FCSTD DOCUMENT  (FreeCAD 0.19R24276 (Git))
Label: Assembly
License: All rights reserved
LicenseURL: http://en.wikipedia.org/wiki/All_rights_reserved
objects: App::Link×6, App::DocumentObjectGroup×2, PartDesign::CoordinateSystem×1, App::FeaturePython×1, App::Part×1
note: 1 computed .brp shape members not serialized (recipe doc carries the construction recipe); baked Part::Feature solids carry a one-line shape summary decoded from their .brp
EXTERNAL_REF file=AssemblyBase.FCStd obj=LCS_Origin
EXTERNAL_REF file=AssemblyBase.FCStd obj=Model
EXTERNAL_REF file=AssemblyArt1.FCStd obj=LCS_Origin
EXTERNAL_REF file=AssemblyBase.FCStd obj=LCS_Art1003
EXTERNAL_REF file=AssemblyArt1.FCStd obj=Model
EXTERNAL_REF file=AssemblyArt1.FCStd obj=LCS_Art2002
EXTERNAL_REF file=AssemblyArt2.FCStd obj=LCS_Art1
EXTERNAL_REF file=AssemblyArt2.FCStd obj=Model
EXTERNAL_REF file=AssemblyArt2.FCStd obj=LCS_Model_1
EXTERNAL_REF file=AssemblyArt3.FCStd obj=LCS_Art2Fix
EXTERNAL_REF file=AssemblyArt3.FCStd obj=Model
EXTERNAL_REF file=AssemblyArt3.FCStd obj=LCS_Art4Fix
EXTERNAL_REF file=AssemblyArt4.FCStd obj=LCS_Art3Fix
EXTERNAL_REF file=AssemblyArt4.FCStd obj=Model
EXTERNAL_REF file=AssemblyArt4.FCStd obj=LCS_Art56Fix
EXTERNAL_REF file=AssemblyArt56.FCStd obj=LCS_Art4Fix
EXTERNAL_REF file=AssemblyArt56.FCStd obj=Model

FEATURE [App::DocumentObjectGroup] Parts
FEATURE [PartDesign::CoordinateSystem] LCS_Origin
  AttacherType = Attacher::AttachEngine3D
  MapMode = 2
  Support = -> [X_Axis]
FEATURE [App::DocumentObjectGroup] Constraints
FEATURE [App::FeaturePython] Variables  # WARN: FeaturePython — macro-defined, semantics opaque (R4)
FEATURE [App::Link] AssemblyBase
  AssemblyType = Asm4EE
  AttachedBy = #LCS_Origin
  AttachedTo = Parent Assembly#LCS_Origin
  LinkedObject = -> <external AssemblyBase.FCStd>#Model
  expr: Placement = LCS_Origin.Placement * AttachmentOffset * AssemblyBase#LCS_Origin.Placement ^ -1
FEATURE [App::Link] AssemblyArt1
  AssemblyType = Asm4EE
  AttachedBy = #LCS_Origin
  AttachedTo = AssemblyBase#LCS_Art1003
  AttachmentOffset = pos=(0,0,0) rot=(0,0,1;4.71239rad)
  LinkPlacement = pos=(0,0,79) rot=(0,0,1;0rad)
  LinkedObject = -> <external AssemblyArt1.FCStd>#Model
  Placement = pos=(0,0,79) rot=(0,0,1;0rad)
  expr: Placement = AssemblyBase.Placement * AssemblyBase#LCS_Art1003.Placement * AttachmentOffset * AssemblyArt1#LCS_Origin.Placement ^ -1
FEATURE [App::Link] AssemblyArt2
  AssemblyType = Asm4EE
  AttachedBy = #LCS_Art1
  AttachedTo = AssemblyArt1#LCS_Art2002
  AttachmentOffset = pos=(0,0,0) rot=(0,0.707107,0.707107;3.14159rad)
  LinkPlacement = pos=(-5.9e-15,-68,202) rot=(0,0.707107,0.707107;3.14159rad)
  LinkedObject = -> <external AssemblyArt2.FCStd>#Model
  Placement = pos=(-5.9e-15,-68,202) rot=(0,0.707107,0.707107;3.14159rad)
  expr: Placement = AssemblyArt1.Placement * AssemblyArt1#LCS_Art2002.Placement * AttachmentOffset * AssemblyArt2#LCS_Art1.Placement ^ -1
FEATURE [App::Link] AssemblyArt3
  AssemblyType = Asm4EE
  AttachedBy = #LCS_Art2Fix
  AttachedTo = AssemblyArt2#LCS_Model_1
  AttachmentOffset = pos=(0,0,0) rot=(1,0,0;1.5708rad)
  LinkPlacement = pos=(-2.09e-14,0,443.5) rot=(0,1,0;3.14159rad)
  LinkedObject = -> <external AssemblyArt3.FCStd>#Model
  Placement = pos=(-2.09e-14,0,443.5) rot=(0,1,0;3.14159rad)
  expr: Placement = AssemblyArt2.Placement * AssemblyArt2#LCS_Model_1.Placement * AttachmentOffset * AssemblyArt3#LCS_Art2Fix.Placement ^ -1
FEATURE [App::Link] AssemblyArt4
  AssemblyType = Asm4EE
  AttachedBy = #LCS_Art3Fix
  AttachedTo = AssemblyArt3#LCS_Art4Fix
  AttachmentOffset = pos=(0,0,0) rot=(0,-1,0;3.14159rad)
  LinkPlacement = pos=(-2.1e-14,0,444.5) rot=(0,0,1;0rad)
  LinkedObject = -> <external AssemblyArt4.FCStd>#Model
  Placement = pos=(-2.1e-14,0,444.5) rot=(0,0,1;0rad)
  expr: Placement = AssemblyArt3.Placement * AssemblyArt3#LCS_Art4Fix.Placement * AttachmentOffset * AssemblyArt4#LCS_Art3Fix.Placement ^ -1
FEATURE [App::Link] AssemblyArt56
  AssemblyType = Asm4EE
  AttachedBy = #LCS_Art4Fix
  AttachedTo = AssemblyArt4#LCS_Art56Fix
  AttachmentOffset = pos=(0,0,0) rot=(0,0,1;1.5708rad)
  LinkPlacement = pos=(-3.07e-14,-1.37e-14,556) rot=(0,0,1;1.5708rad)
  LinkedObject = -> <external AssemblyArt56.FCStd>#Model
  Placement = pos=(-3.07e-14,-1.37e-14,556) rot=(0,0,1;1.5708rad)
  expr: Placement = AssemblyArt4.Placement * AssemblyArt4#LCS_Art56Fix.Placement * AttachmentOffset * AssemblyArt56#LCS_Art4Fix.Placement ^ -1
FEATURE [App::Part] Model
  Configuration = 0
  Group = -> [LCS_Origin,Constraints,Variables,AssemblyBase,AssemblyArt1,AssemblyArt2,AssemblyArt3,AssemblyArt4,AssemblyArt56]
  Origin = -> Origin
  Type = Assembly4 Model

RESOLVED EXTERNAL PARTS (link-assembly join: the EXTERNAL_REF files above that resolve inside this repo's crawl, each included once):
---- part AssemblyArt1.FCStd = doc fcstd_79f823e0a2d4 (58987 chars; too large to inline — full recipe in that document) ----
---- part AssemblyArt2.FCStd = doc fcstd_96a41e5eaa72 (60164 chars; too large to inline — full recipe in that document) ----
---- part AssemblyArt3.FCStd = doc fcstd_8b5b8ba6da66 ----
FCSTD DOCUMENT  (FreeCAD 0.19R24276 (Git))
Label: AssemblyArt3
License: All rights reserved
LicenseURL: http://en.wikipedia.org/wiki/All_rights_reserved
objects: Part::FeaturePython×49, App::Link×14, PartDesign::CoordinateSystem×13, App::Part×7, App::DocumentObjectGroup×6, Part::Feature×5, PartDesign::Line×5, App::FeaturePython×1, Part::Sphere×1
note: 72 computed .brp shape members not serialized (recipe doc carries the construction recipe); baked Part::Feature solids carry a one-line shape summary decoded from their .brp
EXTERNAL_REF file=Art3Body.FCStd obj=LCS_Bottom
EXTERNAL_REF file=Art3Body.FCStd obj=Body002
EXTERNAL_REF file=Art23Optodisk.FCStd obj=LCS_Art23Optodisk
EXTERNAL_REF file=Art3Body.FCStd obj=LCS_OptoDisk
EXTERNAL_REF file=Art23Optodisk.FCStd obj=Body
EXTERNAL_REF file=Art3Body.FCStd obj=LCS_Pulley
EXTERNAL_REF file=Art3Pulley.FCStd obj=LCS_Art3Pulley
EXTERNAL_REF file=Art3Pulley.FCStd obj=Body
EXTERNAL_REF file=Art3Body.FCStd obj=LCS_Art4MotorHolder
EXTERNAL_REF file=Art4MotorFix.FCStd obj=LCS_Art4MotorFix
EXTERNAL_REF file=Art4MotorFix.FCStd obj=Body
EXTERNAL_REF file=Art4MotorFix.FCStd obj=LCS_Art4Motor
EXTERNAL_REF file=Art4MotorGear.FCStd obj=LCS_Art4MotorGear
EXTERNAL_REF file=Art4MotorGear.FCStd obj=Body
EXTERNAL_REF file=Art3Body.FCStd obj=LCS_Fan
EXTERNAL_REF file=Art3Body.FCStd obj=LCS_Bearing
EXTERNAL_REF file=Art3Pulley.FCStd obj=LCS_Bearing
EXTERNAL_REF file=Art3Pulley.FCStd obj=LCS_BearingFix
EXTERNAL_REF file=CommonBearingFixThrough.FCStd obj=LCS_CommonBearingFixThrough
EXTERNAL_REF file=CommonBearingFixThrough.FCStd obj=Body
EXTERNAL_REF file=Art3Body.FCStd obj=LCS_BearingFix
EXTERNAL_REF file=Art3Body.FCStd obj=LCS_OptoSensor
EXTERNAL_REF file=Art4BearingRing.FCStd obj=LCS_Art4BearingRing
EXTERNAL_REF file=Art4BearingRing.FCStd obj=Body
EXTERNAL_REF file=Art4BearingRing.FCStd obj=LCS_BallBearings
EXTERNAL_REF file=Art3Body.FCStd obj=HoleAxis_8
EXTERNAL_REF file=Art3Body.FCStd obj=HoleAxis_9
EXTERNAL_REF file=Art3Body.FCStd obj=HoleAxis_7
EXTERNAL_REF file=Art3Body.FCStd obj=HoleAxis_14
EXTERNAL_REF file=Art3Body.FCStd obj=HoleAxis_11
EXTERNAL_REF file=Art3Body.FCStd obj=HoleAxis_10
EXTERNAL_REF file=Art3Body.FCStd obj=HoleAxis_12
EXTERNAL_REF file=Art3Body.FCStd obj=HoleAxis_13
EXTERNAL_REF file=Art3Pulley.FCStd obj=HoleAxis_6
EXTERNAL_REF file=Art3Pulley.FCStd obj=HoleAxis_5
EXTERNAL_REF file=Art3Pulley.FCStd obj=HoleAxis_3
EXTERNAL_REF file=Art4MotorFix.FCStd obj=HoleAxis_2
EXTERNAL_REF file=Art4MotorFix.FCStd obj=HoleAxis_3
EXTERNAL_REF file=Art4MotorGear.FCStd obj=HoleAxis_2
EXTERNAL_REF file=Art4BearingRing.FCStd obj=HoleAxis_4
EXTERNAL_REF file=Art4BearingRing.FCStd obj=HoleAxis_3
EXTERNAL_REF file=Art4BearingRing.FCStd obj=HoleAxis_1
EXTERNAL_REF file=Art4BearingRing.FCStd obj=HoleAxis_2
EXTERNAL_REF file=CommonBearingFixThrough.FCStd obj=HoleAxis_1
EXTERNAL_REF file=CommonBearingFixThrough.FCStd obj=HoleAxis_2
EXTERNAL_REF file=Art23Optodisk.FCStd obj=HoleAxis_1
EXTERNAL_REF file=Art23Optodisk.FCStd obj=HoleAxis_2
EXTERNAL_REF file=Art3Pulley.FCStd obj=HoleAxis_1
EXTERNAL_REF file=Art3Pulley.FCStd obj=HoleAxis_4
EXTERNAL_REF file=Art3Pulley.FCStd obj=HoleAxis_2
EXTERNAL_REF file=Art3Body.FCStd obj=HoleAxis_2
EXTERNAL_REF file=Art3Body.FCStd obj=HoleAxis_1
EXTERNAL_REF file=Art3Body.FCStd obj=HoleAxis_4
EXTERNAL_REF file=Art3Body.FCStd obj=HoleAxis_3
EXTERNAL_REF file=Art3Body.FCStd obj=HoleAxis_18
EXTERNAL_REF file=Art3Body.FCStd obj=HoleAxis_17
EXTERNAL_REF file=Art3Body.FCStd obj=HoleAxis_16
EXTERNAL_REF file=Art3Body.FCStd obj=HoleAxis_15
EXTERNAL_REF file=Art4MotorFix.FCStd obj=HoleAxis_5
EXTERNAL_REF file=Art4MotorFix.FCStd obj=HoleAxis_6
EXTERNAL_REF file=Art4MotorFix.FCStd obj=HoleAxis_4
EXTERNAL_REF file=Art4MotorFix.FCStd obj=HoleAxis_1
EXTERNAL_REF file=Art3Body.FCStd obj=HoleAxis_6
EXTERNAL_REF file=Art3Body.FCStd obj=HoleAxis_5
EXTERNAL_REF file=Art4MotorGear.FCStd obj=HoleAxis_1

FEATURE [PartDesign::CoordinateSystem] LCS_Origin
  AttacherType = Attacher::AttachEngine3D
  MapMode = 2
  Support = -> [X_Axis]
FEATURE [App::DocumentObjectGroup] Constraints
FEATURE [App::FeaturePython] Variables  # WARN: FeaturePython — macro-defined, semantics opaque (R4)
FEATURE [App::Link] Art3Body_Art3Body
  AssemblyType = Asm4EE
  AttachedBy = #LCS_Art3Body
  AttachedTo = Parent Assembly#LCS_Origin
  LinkPlacement = pos=(-6.7e-15,2.7e-15,-7) rot=(0,0,1;0rad)
  LinkedObject = -> <external Art3Body.FCStd>#Body002
  Placement = pos=(-6.7e-15,2.7e-15,-7) rot=(0,0,1;0rad)
  expr: Placement = LCS_Origin.Placement * AttachmentOffset * Art3Body#<<LCS_Art3Body>>.Placement ^ -1
FEATURE [App::Link] Art23Optodisk_Art23Optodisk
  AssemblyType = Asm4EE
  AttachedBy = #LCS_Art23Optodisk
  AttachedTo = Art3Body_Art3Body#LCS_OptoRing
  AttachmentOffset = pos=(0,0,0) rot=(0,0,1;3.14159rad)
  LinkPlacement = pos=(-3.27e-14,35,81.5) rot=(1,0,0;4.71239rad)
  LinkedObject = -> <external Art23Optodisk.FCStd>#Body
  Placement = pos=(-3.27e-14,35,81.5) rot=(1,0,0;4.71239rad)
  expr: Placement = Art3Body_Art3Body.Placement * Art3Body#<<LCS_OptoRing>>.Placement * AttachmentOffset * Art23Optodisk#LCS_Art23Optodisk.Placement ^ -1
FEATURE [App::Link] Art3Pulley_Art3Pulley
  AssemblyType = Asm4EE
  AttachedBy = #LCS_Art3Pulley
  AttachedTo = Art3Body_Art3Body#LCS_Pulley
  LinkPlacement = pos=(-2.65e-14,-53,81.5) rot=(-1,0,0;1.5708rad)
  LinkedObject = -> <external Art3Pulley.FCStd>#Body
  Placement = pos=(-2.65e-14,-53,81.5) rot=(-1,0,0;1.5708rad)
  expr: Placement = Art3Body_Art3Body.Placement * Art3Body#LCS_Pulley.Placement * AttachmentOffset * Art3Pulley#LCS_Art3Pulley.Placement ^ -1
FEATURE [App::Link] Art4MotorFix_Art4MotorFix
  AssemblyType = Asm4EE
  AttachedBy = #LCS_Art4MotorFix
  AttachedTo = Art3Body_Art3Body#LCS_MotorHolder
  AttachmentOffset = pos=(0,0,0) rot=(0,-1,0;3.14159rad)
  LinkPlacement = pos=(27.85,-1.36e-14,82.6) rot=(0,1,0;3.14159rad)
  LinkedObject = -> <external Art4MotorFix.FCStd>#Body
  Placement = pos=(27.85,-1.36e-14,82.6) rot=(0,1,0;3.14159rad)
  expr: Placement = Art3Body_Art3Body.Placement * Art3Body#<<LCS_MotorHolder>>.Placement * AttachmentOffset * Art4MotorFix#LCS_Art4MotorFix.Placement ^ -1
FEATURE [PartDesign::CoordinateSystem] LCS_0008
  AttacherType = Attacher::AttachEngine3D
  MapMode = 2
  Support = -> [X_Axis009]
FEATURE [Part::Feature] Part__Feature031  label="Nema-17-motor-40mm-final"
  shape: bbox 42.3 x 42.3 x 60.1 mm, 55 faces (baked)
FEATURE [PartDesign::CoordinateSystem] LCS_Stepper_Nema17x40
  AttacherType = Attacher::AttachEngine3D
  MapMode = 45
  Placement = pos=(7.5e-15,0,0) rot=(0,0,1;0rad)
  Support = -> [Part__Feature031]
FEATURE [PartDesign::CoordinateSystem] LCS_Gear2  label="LCS_Gear"
  AttacherType = Attacher::AttachEngine3D
  AttachmentOffset = pos=(0,0,1.9) rot=(0,0,1;0rad)
  MapMode = 11
  Placement = pos=(0,0,44) rot=(0,0,1;1.5708rad)
  Support = -> [Part__Feature031]
FEATURE [App::Part] Stepper_Nema17x40
  Group = -> [LCS_0008,Part__Feature031,LCS_Stepper_Nema17x40,LCS_Gear2]
  Origin = -> Origin009
FEATURE [Part::Feature] Cut001
  shape: bbox 27.6 x 11 x 11.5 mm, 43 faces (baked)
FEATURE [PartDesign::CoordinateSystem] LCS_OpticSensor
  AttacherType = Attacher::AttachEngine3D
  MapMode = 11
  Placement = pos=(14,0,0) rot=(0,0,1;1.5708rad)
  Support = -> [Cut001]
FEATURE [PartDesign::Line] HoleAxis_1
  AttacherType = Attacher::AttachEngineLine
  Length = 4.2272
  MapMode = 19
  Placement = pos=(14,0,1.5) rot=(0,0,1;0rad)
  ResizeMode = 1
  Support = -> [Cut001]
FEATURE [App::Part] Part  label="OpticSensor"
  Group = -> [Cut001,LCS_OpticSensor,HoleAxis_1]
  Origin = -> Origin010
FEATURE [Part::Feature] Chamfer_solid  label="NEMA-17_Stepper_Motor_34mm"
  shape: bbox 42.3 x 42.3 x 54 mm, 55 faces (baked)
FEATURE [PartDesign::CoordinateSystem] LCS_Stepper_Nema17x34
  AttacherType = Attacher::AttachEngine3D
  MapMode = 45
  Placement = pos=(7.4e-15,0,34) rot=(0,0,1;0rad)
  Support = -> [Chamfer_solid]
FEATURE [PartDesign::CoordinateSystem] LCS_Gear  label="LCS_Gear001"
  AttacherType = Attacher::AttachEngine3D
  AttachmentOffset = pos=(0,0,4) rot=(0,0,1;0rad)
  MapMode = 11
  Placement = pos=(0,0,40) rot=(0,0,1;1.5708rad)
  Support = -> [Chamfer_solid]
FEATURE [App::Part] Stepper_Nema17x34
  Group = -> [Chamfer_solid,LCS_Stepper_Nema17x34,LCS_Gear]
  Origin = -> Origin011
FEATURE [App::DocumentObjectGroup] Group  label="Electronics"
  Group = -> [Stepper_Nema17x40,Part,Stepper_Nema17x34]
FEATURE [App::Link] Stepper_Nema17x34001
  AssemblyType = Asm4EE
  AttachedBy = #LCS_Stepper_Nema17x34
  AttachedTo = Art4MotorFix_Art4MotorFix#LCS_Art4Motor
  LinkPlacement = pos=(27.85,-1.179e-13,116.6) rot=(0,1,0;3.14159rad)
  LinkedObject = -> Stepper_Nema17x34
  Placement = pos=(27.85,-1.179e-13,116.6) rot=(0,1,0;3.14159rad)
  expr: Placement = Art4MotorFix_Art4MotorFix.Placement * Art4MotorFix#LCS_Art4Motor.Placement * AttachmentOffset * LCS_Stepper_Nema17x34.Placement ^ -1
FEATURE [App::Link] Art4MotorGear_Art4MotorGear
  AssemblyType = Asm4EE
  AttachedBy = #LCS_Art4MotorGear
  AttachedTo = Stepper_Nema17x34001#LCS_Gear
  AttachmentOffset = pos=(0,0,0) rot=(0,1,0;3.14159rad)
  LinkPlacement = pos=(27.85,3.49e-14,66.6) rot=(0,-1,0;3.14159rad)
  LinkedObject = -> <external Art4MotorGear.FCStd>#Body
  Placement = pos=(27.85,3.49e-14,66.6) rot=(0,-1,0;3.14159rad)
  expr: Placement = Stepper_Nema17x34001.Placement * LCS_Gear.Placement * AttachmentOffset * Art4MotorGear#LCS_Art4MotorGear.Placement ^ -1
FEATURE [Part::Feature] Part__Feature001  label="fan-40x40mm"
  shape: bbox 40 x 40 x 10 mm, 172 faces (baked)
FEATURE [PartDesign::Line] HoleAxis_8
  AttacherType = Attacher::AttachEngineLine
  Length = 6.05899
  MapMode = 19
  Placement = pos=(-15.9948,15.9948,6.76) rot=(0,0,1;0rad)
  ResizeMode = 1
  Support = -> [Part__Feature001]
FEATURE [PartDesign::Line] HoleAxis_5
  AttacherType = Attacher::AttachEngineLine
  Length = 6.05899
  MapMode = 19
  Placement = pos=(15.9948,15.9948,6.76) rot=(0,0,1;4.71239rad)
  ResizeMode = 1
  Support = -> [Part__Feature001]
FEATURE [PartDesign::Line] HoleAxis_7
  AttacherType = Attacher::AttachEngineLine
  Length = 6.05899
  MapMode = 19
  Placement = pos=(-15.9948,-15.9948,6.76) rot=(0,0,1;1.5708rad)
  ResizeMode = 1
  Support = -> [Part__Feature001]
FEATURE [PartDesign::Line] HoleAxis_6
  AttacherType = Attacher::AttachEngineLine
  Length = 6.05899
  MapMode = 19
  Placement = pos=(15.9948,-15.9948,6.76) rot=(0,0,1;3.14159rad)
  ResizeMode = 1
  Support = -> [Part__Feature001]
FEATURE [PartDesign::CoordinateSystem] LCS_0001
  AttacherType = Attacher::AttachEngine3D
  MapMode = 2
  Support = -> [X_Axis002]
FEATURE [PartDesign::CoordinateSystem] LCS_Fan001
  AttacherType = Attacher::AttachEngine3D
  AttachmentOffset = pos=(0,0,-2.21) rot=(0,0,1;0rad)
  MapMode = 45
  Placement = pos=(-5e-16,5e-16,-4e-16) rot=(0,0,1;0rad)
  Support = -> [Part__Feature001]
FEATURE [App::Part] Fan_40x40
  Group = -> [LCS_0001,Part__Feature001,LCS_Fan001,HoleAxis_5,HoleAxis_6,HoleAxis_7,HoleAxis_8]
  Origin = -> Origin002
FEATURE [App::DocumentObjectGroup] Group001  label="Fans"
  Group = -> [Fan_40x40]
FEATURE [App::Link] Fan_40x40001
  AssemblyType = Asm4EE
  AttachedBy = #LCS_Fan001
  AttachedTo = Art3Body_Art3Body#LCS_Fan
  AttachmentOffset = pos=(0,0,0) rot=(0,0,1;3.14159rad)
  LinkPlacement = pos=(-46,1.23e-14,99) rot=(0.57735,-0.57735,0.57735;4.18879rad)
  LinkedObject = -> Fan_40x40
  Placement = pos=(-46,1.23e-14,99) rot=(0.57735,-0.57735,0.57735;4.18879rad)
  expr: Placement = Art3Body_Art3Body.Placement * Art3Body#LCS_Fan.Placement * AttachmentOffset * LCS_Fan001.Placement ^ -1
FEATURE [Part::Feature] Compound001  label="Bearing 625ZZ"
  shape: bbox 16 x 16 x 5 mm, 86 faces, 3 solids (baked)
FEATURE [PartDesign::CoordinateSystem] LCS_0
  AttacherType = Attacher::AttachEngine3D
  MapMode = 2
  Support = -> [X_Axis003]
FEATURE [App::Part] Bearing_625ZZ
  Group = -> [LCS_0,Compound001]
  Origin = -> Origin003
FEATURE [App::Link] Bearing_625ZZ001
  AssemblyType = Asm4EE
  AttachedBy = #LCS_0
  AttachedTo = Art3Body_Art3Body#LCS_Bearing
  LinkPlacement = pos=(-3.9e-15,32,81.5) rot=(0.57735,0.57735,0.57735;4.18879rad)
  LinkedObject = -> Bearing_625ZZ
  Placement = pos=(-3.9e-15,32,81.5) rot=(0.57735,0.57735,0.57735;4.18879rad)
  expr: Placement = Art3Body_Art3Body.Placement * Art3Body#LCS_Bearing.Placement * AttachmentOffset * LCS_0.Placement ^ -1
FEATURE [App::Link] Bearing_625ZZ002
  AssemblyType = Asm4EE
  AttachedBy = #LCS_0
  AttachedTo = Art3Pulley_Art3Pulley#LCS_Bearing
  AttachmentOffset = pos=(0,0,0) rot=(0,1,0;3.14159rad)
  LinkPlacement = pos=(-2.5e-14,-44,81.5) rot=(0.57735,0.57735,-0.57735;2.0944rad)
  LinkedObject = -> Bearing_625ZZ
  Placement = pos=(-2.5e-14,-44,81.5) rot=(0.57735,0.57735,-0.57735;2.0944rad)
  expr: Placement = Art3Pulley_Art3Pulley.Placement * Art3Pulley#LCS_Bearing.Placement * AttachmentOffset * LCS_0.Placement ^ -1
FEATURE [App::Link] CommonBearingFixThrough_CommonBearingFixThrough
  AssemblyType = Asm4EE
  AttachedBy = #LCS_CommonBearingFixThrough
  AttachedTo = Art3Pulley_Art3Pulley#LCS_BearingFix
  AttachmentOffset = pos=(0,0,0) rot=(0,1,0;3.14159rad)
  LinkPlacement = pos=(-2.62e-14,-49,81.5) rot=(-1,0,0;4.71239rad)
  LinkedObject = -> <external CommonBearingFixThrough.FCStd>#Body
  Placement = pos=(-2.62e-14,-49,81.5) rot=(-1,0,0;4.71239rad)
  expr: Placement = Art3Pulley_Art3Pulley.Placement * Art3Pulley#LCS_BearingFix.Placement * AttachmentOffset * CommonBearingFixThrough#LCS_CommonBearingFixThrough.Placement ^ -1
FEATURE [App::Link] CommonBearingFixThrough_CommonBearingFixThrough001
  AssemblyType = Asm4EE
  AttachedBy = #LCS_CommonBearingFixThrough
  AttachedTo = Art3Body_Art3Body#LCS_BearingFix
  LinkPlacement = pos=(-1.61e-14,37,81.5) rot=(-0.57735,-0.57735,-0.57735;2.0944rad)
  LinkedObject = -> <external CommonBearingFixThrough.FCStd>#Body
  Placement = pos=(-1.61e-14,37,81.5) rot=(-0.57735,-0.57735,-0.57735;2.0944rad)
  expr: Placement = Art3Body_Art3Body.Placement * Art3Body#LCS_BearingFix.Placement * AttachmentOffset * CommonBearingFixThrough#LCS_CommonBearingFixThrough.Placement ^ -1
FEATURE [App::Link] OpticSensor  label="OpticSensor001"
  AssemblyType = Asm4EE
  AttachedBy = #LCS_OpticSensor
  AttachedTo = Art3Body_Art3Body#LCS_OptoSensor
  AttachmentOffset = pos=(0,0,0) rot=(0,0,1;3.14159rad)
  LinkPlacement = pos=(-32.4,-1e-16,23.5) rot=(0,-1,0;3.14159rad)
  LinkedObject = -> Part
  Placement = pos=(-32.4,-1e-16,23.5) rot=(0,-1,0;3.14159rad)
  expr: Placement = Art3Body_Art3Body.Placement * Art3Body#LCS_OptoSensor.Placement * AttachmentOffset * LCS_OpticSensor.Placement ^ -1
FEATURE [App::Link] Art4BearingRing_Art4BearingRing
  AssemblyType = Asm4EE
  AttachedBy = #LCS_Art4BearingRing
  AttachedTo = Art3Body_Art3Body#LCS_Bottom
  AttachmentOffset = pos=(0,0,4) rot=(0.707107,-0.707107,0;3.14159rad)
  LinkPlacement = pos=(-5e-16,0,4) rot=(0.707107,-0.707107,0;3.14159rad)
  LinkedObject = -> <external Art4BearingRing.FCStd>#Body
  Placement = pos=(-5e-16,0,4) rot=(0.707107,-0.707107,0;3.14159rad)
  expr: Placement = Art3Body_Art3Body.Placement * Art3Body#LCS_Bottom.Placement * AttachmentOffset * Art4BearingRing#LCS_Art4BearingRing.Placement ^ -1
FEATURE [Part::Sphere] Sphere
  Angle1 = -90
  Angle2 = 90
  Angle3 = 360
  AttacherType = Attacher::AttachEngine3D
  Placement = pos=(35,0,0) rot=(0,0,1;0rad)
  Radius = 3
FEATURE [Part::FeaturePython] Array  # Draft array (typed FeaturePython)
  Angle = 360
  ArrayType = 1
  Axis = (0,0,1)
  Base = -> Sphere
  Center = (0,0,0)
  Count = 36
  ExpandArray = false
  Fuse = false
  IntervalAxis = (0,0,0)
  IntervalX = (50,0,0)
  IntervalY = (0,50,0)
  IntervalZ = (0,0,50)
  NumberCircles = 3
  NumberPolar = 36
  NumberX = 2
  NumberY = 2
  NumberZ = 1
  PlacementList = 36 placements: [(35,0,0),(34.4683,6.07769,0),(32.8892,11.9707,0),(30.3109,17.5,0),(26.8116,22.4976,0),(22.4976,26.8116,0),(17.5,30.3109,0),(11.9707,32.8892,0),(6.07769,34.4683,0),(0,35,0),(-6.07769,34.4683,0),(-11.9707,32.8892,0),(-17.5,30.3109,0),(-22.4976,26.8116,0),(-26.8116,22.4976,0),(-30.3109,17.5,0),(-32.8892,11.9707,0),(-34.4683,6.07769,0),(-35,4.28626e-15,0),(-34.4683,-6.07769,0),(-32.8892,-11.9707,0),+15 more]
  RadialDistance = 50
  ScaleList = (36) [(1,1,1),(1,1,1),(1,1,1),(1,1,1),(1,1,1),(1,1,1),(1,1,1),(1,1,1),(1,1,1),(1,1,1),(1,1,1),(1,1,1),(1,1,1),(1,1,1),(1,1,1),(1,1,1),(1,1,1),(1,1,1),+18 more]
  Symmetry = 1
  TangentialDistance = 25
FEATURE [PartDesign::CoordinateSystem] LCS_BearingBalls
  AttacherType = Attacher::AttachEngine3D
FEATURE [App::Part] Part001  label="BearingBalls"
  Group = -> [Sphere,Array,LCS_BearingBalls]
  Origin = -> Origin012
FEATURE [App::DocumentObjectGroup] Group002  label="Bearing"
  Group = -> [Bearing_625ZZ,Part001]
FEATURE [App::DocumentObjectGroup] Parts
  Group = -> [Group,Group001,Group002]
FEATURE [App::Link] BearingBalls  label="BearingBalls001"
  AssemblyType = Asm4EE
  AttachedBy = #LCS_BearingBalls
  AttachedTo = Art4BearingRing_Art4BearingRing#LCS_BallBearings
  AttachmentOffset = pos=(0,0,1) rot=(0,0,1;0rad)
  LinkPlacement = pos=(-3e-16,-7e-16,-1) rot=(0.707107,-0.707107,0;3.14159rad)
  LinkedObject = -> Part001
  Placement = pos=(-3e-16,-7e-16,-1) rot=(0.707107,-0.707107,0;3.14159rad)
  expr: Placement = Art4BearingRing_Art4BearingRing.Placement * Art4BearingRing#LCS_BallBearings.Placement * AttachmentOffset * LCS_BearingBalls.Placement ^ -1
FEATURE [Part::FeaturePython] Nut  label="M3-Nut"  # Fasteners workbench fastener (typed FeaturePython)
  AssemblyType = Asm4EE
  AttachedBy = Origin
  AttachedTo = Art3Body_Art3Body#HoleAxis_8
  AttachmentOffset = pos=(0,0,0) rot=(0,0,1;1.5708rad)
  Placement = pos=(-16,-30,68.5) rot=(0.57735,0.57735,0.57735;4.18879rad)
  diameter = 4
  invert = false
  matchOuter = false
  offset = 0
  thread = false
  type = 7
  expr: Placement = Art3Body_Art3Body.Placement * Art3Body#HoleAxis_8.Placement * AttachmentOffset
FEATURE [Part::FeaturePython] Nut001  label="M3-Nut022"  # Fasteners workbench fastener (typed FeaturePython)
  AssemblyType = Asm4EE
  AttachedBy = Origin
  AttachedTo = Art3Body_Art3Body#HoleAxis_9
  AttachmentOffset = pos=(0,0,0) rot=(0,0,1;1.5708rad)
  Placement = pos=(-1.2e-14,-30,99.5) rot=(0.57735,0.57735,0.57735;4.18879rad)
  diameter = 4
  invert = false
  matchOuter = false
  offset = 0
  thread = false
  type = 7
  expr: Placement = Art3Body_Art3Body.Placement * Art3Body#HoleAxis_9.Placement * AttachmentOffset
FEATURE [Part::FeaturePython] Nut002  label="M3-Nut023"  # Fasteners workbench fastener (typed FeaturePython)
  AssemblyType = Asm4EE
  AttachedBy = Origin
  AttachedTo = Art3Body_Art3Body#HoleAxis_7
  AttachmentOffset = pos=(0,0,0) rot=(0,0,1;1.5708rad)
  Placement = pos=(16,-30,68.5) rot=(0.57735,0.57735,0.57735;4.18879rad)
  diameter = 4
  invert = false
  matchOuter = false
  offset = 0
  thread = false
  type = 7
  expr: Placement = Art3Body_Art3Body.Placement * Art3Body#HoleAxis_7.Placement * AttachmentOffset
FEATURE [Part::FeaturePython] Nut003  label="M3-Nut024"  # Fasteners workbench fastener (typed FeaturePython)
  AssemblyType = Asm4EE
  AttachedBy = Origin
  AttachedTo = Art3Body_Art3Body#HoleAxis_14
  AttachmentOffset = pos=(0,0,0) rot=(1,0,0;3.14159rad)
  Placement = pos=(-46.4,-3e-15,25.35) rot=(0,0,1;0rad)
  diameter = 4
  invert = false
  matchOuter = false
  offset = 0
  thread = false
  type = 7
  expr: Placement = Art3Body_Art3Body.Placement * Art3Body#HoleAxis_14.Placement * AttachmentOffset
FEATURE [Part::FeaturePython] Nut004  label="M3-Nut025"  # Fasteners workbench fastener (typed FeaturePython)
  AssemblyType = Asm4EE
  AttachedBy = Origin
  AttachedTo = Art3Body_Art3Body#HoleAxis_11
  AttachmentOffset = pos=(0,0,0) rot=(-1,0,0;3.14159rad)
  Placement = pos=(25,33,78) rot=(0,0.707107,-0.707107;3.14159rad)
  diameter = 4
  invert = false
  matchOuter = false
  offset = 0
  thread = false
  type = 7
  expr: Placement = Art3Body_Art3Body.Placement * Art3Body#HoleAxis_11.Placement * AttachmentOffset
FEATURE [Part::FeaturePython] Nut005  label="M3-Nut026"  # Fasteners workbench fastener (typed FeaturePython)
  AssemblyType = Asm4EE
  AttachedBy = Origin
  AttachedTo = Art3Body_Art3Body#HoleAxis_10
  AttachmentOffset = pos=(0,0,0) rot=(1,0,0;3.14159rad)
  Placement = pos=(-8e-15,33,70.5) rot=(0,0.707107,-0.707107;3.14159rad)
  diameter = 4
  invert = false
  matchOuter = false
  offset = 0
  thread = false
  type = 7
  expr: Placement = Art3Body_Art3Body.Placement * Art3Body#HoleAxis_10.Placement * AttachmentOffset
FEATURE [Part::FeaturePython] Nut006  label="M3-Nut027"  # Fasteners workbench fastener (typed FeaturePython)
  AssemblyType = Asm4EE
  AttachedBy = Origin
  AttachedTo = Art3Body_Art3Body#HoleAxis_12
  AttachmentOffset = pos=(0,0,0) rot=(1,0,0;3.14159rad)
  Placement = pos=(-25,33,78) rot=(0,0.707107,-0.707107;3.14159rad)
  diameter = 4
  invert = false
  matchOuter = false
  offset = 0
  thread = false
  type = 7
  expr: Placement = Art3Body_Art3Body.Placement * Art3Body#HoleAxis_12.Placement * AttachmentOffset
FEATURE [Part::FeaturePython] Nut007  label="M3-Nut028"  # Fasteners workbench fastener (typed FeaturePython)
  AssemblyType = Asm4EE
  AttachedBy = Origin
  AttachedTo = Art3Body_Art3Body#HoleAxis_13
  AttachmentOffset = pos=(0,0,0) rot=(1,0,0;3.14159rad)
  Placement = pos=(-9e-15,33,92.5) rot=(0,0.707107,-0.707107;3.14159rad)
  diameter = 4
  invert = false
  matchOuter = false
  offset = 0
  thread = false
  type = 7
  expr: Placement = Art3Body_Art3Body.Placement * Art3Body#HoleAxis_13.Placement * AttachmentOffset
FEATURE [Part::FeaturePython] Nut008  label="M3-Nut029"  # Fasteners workbench fastener (typed FeaturePython)
  AssemblyType = Asm4EE
  AttachedBy = Origin
  AttachedTo = Art3Pulley_Art3Pulley#HoleAxis_6
  AttachmentOffset = pos=(0,0,0) rot=(0.707107,-0.707107,0;3.14159rad)
  Placement = pos=(-11,-46,81.5) rot=(0.57735,-0.57735,-0.57735;4.18879rad)
  diameter = 4
  invert = false
  matchOuter = false
  offset = 0
  thread = false
  type = 7
  expr: Placement = Art3Pulley_Art3Pulley.Placement * Art3Pulley#HoleAxis_6.Placement * AttachmentOffset
FEATURE [Part::FeaturePython] Nut009  label="M3-Nut030"  # Fasteners workbench fastener (typed FeaturePython)
  AssemblyType = Asm4EE
  AttachedBy = Origin
  AttachedTo = Art3Pulley_Art3Pulley#HoleAxis_5
  AttachmentOffset = pos=(0,0,0) rot=(0.707107,0.707107,0;3.14159rad)
  Placement = pos=(11,-46,81.5) rot=(0.57735,0.57735,0.57735;4.18879rad)
  diameter = 4
  invert = false
  matchOuter = false
  offset = 0
  thread = false
  type = 7
  expr: Placement = Art3Pulley_Art3Pulley.Placement * Art3Pulley#HoleAxis_5.Placement * AttachmentOffset
FEATURE [Part::FeaturePython] Nut010  label="M3-Nut031"  # Fasteners workbench fastener (typed FeaturePython)
  AssemblyType = Asm4EE
  AttachedBy = Origin
  AttachedTo = Art3Pulley_Art3Pulley#HoleAxis_3
  AttachmentOffset = pos=(0,0,0) rot=(0.707107,-0.707107,0;3.14159rad)
  Placement = pos=(-2.2e-14,-46.5,54.15) rot=(0,0,1;1.5708rad)
  diameter = 4
  invert = false
  matchOuter = false
  offset = 0
  thread = false
  type = 7
  expr: Placement = Art3Pulley_Art3Pulley.Placement * Art3Pulley#HoleAxis_3.Placement * AttachmentOffset
FEATURE [Part::FeaturePython] Nut011  label="M3-Nut032"  # Fasteners workbench fastener (typed FeaturePython)
  AssemblyType = Asm4EE
  AttachedBy = Origin
  AttachedTo = Art4MotorFix_Art4MotorFix#HoleAxis_2
  AttachmentOffset = pos=(0,0,0) rot=(0.707107,-0.707107,0;3.14159rad)
  Placement = pos=(48,-4.5,77.6) rot=(0,-1,0;1.5708rad)
  diameter = 4
  invert = false
  matchOuter = false
  offset = 0
  thread = false
  type = 7
  expr: Placement = Art4MotorFix_Art4MotorFix.Placement * Art4MotorFix#HoleAxis_2.Placement * AttachmentOffset
FEATURE [Part::FeaturePython] Nut012  label="M3-Nut033"  # Fasteners workbench fastener (typed FeaturePython)
  AssemblyType = Asm4EE
  AttachedBy = Origin
  AttachedTo = Art4MotorFix_Art4MotorFix#HoleAxis_3
  AttachmentOffset = pos=(0,0,0) rot=(0.707107,-0.707107,0;3.14159rad)
  Placement = pos=(48,4.5,77.6) rot=(0,-1,0;1.5708rad)
  diameter = 4
  invert = false
  matchOuter = false
  offset = 0
  thread = false
  type = 7
  expr: Placement = Art4MotorFix_Art4MotorFix.Placement * Art4MotorFix#HoleAxis_3.Placement * AttachmentOffset
FEATURE [Part::FeaturePython] Nut013  label="M3-Nut050"  # Fasteners workbench fastener (typed FeaturePython)
  AssemblyType = Asm4EE
  AttachedBy = Origin
  AttachedTo = Art4MotorGear_Art4MotorGear#HoleAxis_2
  AttachmentOffset = pos=(0,0,0) rot=(0,0,1;1.5708rad)
  Placement = pos=(35.35,2.6e-14,71.1) rot=(0.707107,0,-0.707107;3.14159rad)
  diameter = 4
  invert = false
  matchOuter = false
  offset = 0
  thread = false
  type = 7
  expr: Placement = Art4MotorGear_Art4MotorGear.Placement * Art4MotorGear#HoleAxis_2.Placement * AttachmentOffset
FEATURE [Part::FeaturePython] Nut014  label="M3-Nut035"  # Fasteners workbench fastener (typed FeaturePython)
  AssemblyType = Asm4EE
  AttachedBy = Origin
  AttachedTo = Art4BearingRing_Art4BearingRing#HoleAxis_4
  Placement = pos=(22.5,-39,-3.5) rot=(0.707107,0.707107,0;3.14159rad)
  diameter = 4
  invert = false
  matchOuter = false
  offset = 0
  thread = false
  type = 7
  expr: Placement = Art4BearingRing_Art4BearingRing.Placement * Art4BearingRing#HoleAxis_4.Placement * AttachmentOffset
FEATURE [Part::FeaturePython] Nut015  label="M3-Nut036"  # Fasteners workbench fastener (typed FeaturePython)
  AssemblyType = Asm4EE
  AttachedBy = Origin
  AttachedTo = Art4BearingRing_Art4BearingRing#HoleAxis_3
  Placement = pos=(22.5,39,-3.5) rot=(0.707107,0.707107,0;3.14159rad)
  diameter = 4
  invert = false
  matchOuter = false
  offset = 0
  thread = false
  type = 7
  expr: Placement = Art4BearingRing_Art4BearingRing.Placement * Art4BearingRing#HoleAxis_3.Placement * AttachmentOffset
FEATURE [Part::FeaturePython] Nut016  label="M3-Nut037"  # Fasteners workbench fastener (typed FeaturePython)
  AssemblyType = Asm4EE
  AttachedBy = Origin
  AttachedTo = Art4BearingRing_Art4BearingRing#HoleAxis_1
  Placement = pos=(-22.5,-39,-3.5) rot=(0.707107,0.707107,0;3.14159rad)
  diameter = 4
  invert = false
  matchOuter = false
  offset = 0
  thread = false
  type = 7
  expr: Placement = Art4BearingRing_Art4BearingRing.Placement * Art4BearingRing#HoleAxis_1.Placement * AttachmentOffset
FEATURE [Part::FeaturePython] Nut017  label="M3-Nut038"  # Fasteners workbench fastener (typed FeaturePython)
  AssemblyType = Asm4EE
  AttachedBy = Origin
  AttachedTo = Art4BearingRing_Art4BearingRing#HoleAxis_2
  Placement = pos=(-22.5,39,-3.5) rot=(0.707107,0.707107,0;3.14159rad)
  diameter = 4
  invert = false
  matchOuter = false
  offset = 0
  thread = false
  type = 7
  expr: Placement = Art4BearingRing_Art4BearingRing.Placement * Art4BearingRing#HoleAxis_2.Placement * AttachmentOffset
FEATURE [Part::FeaturePython] Nut018  label="M3-Nut051"  # Fasteners workbench fastener (typed FeaturePython)
  AssemblyType = Asm4EE
  AttachedBy = Origin
  AttachedTo = Fan_40x40001#HoleAxis_7
  AttachmentOffset = pos=(0,0,0) rot=(0,0,-1;3.14159rad)
  Placement = pos=(-39.24,15.9948,114.995) rot=(0.707107,0,0.707107;3.14159rad)
  diameter = 4
  invert = false
  matchOuter = false
  offset = 0
  thread = false
  type = 7
  expr: Placement = Fan_40x40001.Placement * HoleAxis_7.Placement * AttachmentOffset
FEATURE [Part::FeaturePython] Nut019  label="M3-Nut048"  # Fasteners workbench fastener (typed FeaturePython)
  AssemblyType = Asm4EE
  AttachedBy = Origin
  AttachedTo = Fan_40x40001#HoleAxis_8
  Placement = pos=(-39.24,15.9948,83.0052) rot=(0.57735,-0.57735,0.57735;4.18879rad)
  diameter = 4
  invert = false
  matchOuter = false
  offset = 0
  thread = false
  type = 7
  expr: Placement = Fan_40x40001.Placement * HoleAxis_8.Placement * AttachmentOffset
FEATURE [Part::FeaturePython] Nut020  label="M3-Nut052"  # Fasteners workbench fastener (typed FeaturePython)
  AssemblyType = Asm4EE
  AttachedBy = Origin
  AttachedTo = Fan_40x40001#HoleAxis_6
  Placement = pos=(-39.24,-15.9948,114.995) rot=(0.57735,0.57735,0.57735;2.0944rad)
  diameter = 4
  invert = false
  matchOuter = false
  offset = 0
  thread = false
  type = 7
  expr: Placement = Fan_40x40001.Placement * HoleAxis_6.Placement * AttachmentOffset
FEATURE [Part::FeaturePython] Nut021  label="M3-Nut049"  # Fasteners workbench fastener (typed FeaturePython)
  AssemblyType = Asm4EE
  AttachedBy = Origin
  AttachedTo = Fan_40x40001#HoleAxis_5
  Placement = pos=(-39.24,-15.9948,83.0052) rot=(0.707107,0,0.707107;3.14159rad)
  diameter = 4
  invert = false
  matchOuter = false
  offset = 0
  thread = false
  type = 7
  expr: Placement = Fan_40x40001.Placement * HoleAxis_5.Placement * AttachmentOffset
FEATURE [Part::FeaturePython] Screw  label="M3x8-Screw"  # Fasteners workbench fastener (typed FeaturePython)
  AssemblyType = Asm4EE
  AttachedBy = Origin
  AttachedTo = OpticSensor#HoleAxis_1
  Placement = pos=(-46.4,-3e-15,22) rot=(0,1,0;3.14159rad)
  diameter = 4
  invert = false
  length = 2
  lengthCustom = 8
  matchOuter = false
  offset = 0
  thread = false
  type = 33
  expr: Placement = OpticSensor.Placement * HoleAxis_1.Placement * AttachmentOffset
FEATURE [Part::FeaturePython] Screw001  label="M3x8-Screw005"  # Fasteners workbench fastener (typed FeaturePython)
  AssemblyType = Asm4EE
  AttachedBy = Origin
  AttachedTo = CommonBearingFixThrough_CommonBearingFixThrough001#HoleAxis_1
  AttachmentOffset = pos=(0,0,0) rot=(1,0,0;3.14159rad)
  Placement = pos=(-1.6e-14,38,70.5) rot=(-0.57735,-0.57735,-0.57735;2.0944rad)
  diameter = 4
  invert = false
  length = 2
  lengthCustom = 8
  matchOuter = false
  offset = 0
  thread = false
  type = 33
  expr: Placement = CommonBearingFixThrough_CommonBearingFixThrough001.Placement * CommonBearingFixThrough#HoleAxis_1.Placement * AttachmentOffset
FEATURE [Part::FeaturePython] Screw002  label="M3x8-Screw006"  # Fasteners workbench fastener (typed FeaturePython)
  AssemblyType = Asm4EE
  AttachedBy = Origin
  AttachedTo = CommonBearingFixThrough_CommonBearingFixThrough001#HoleAxis_2
  AttachmentOffset = pos=(0,0,0) rot=(-1,0,0;3.14159rad)
  Placement = pos=(-1.6e-14,38,92.5) rot=(-0.57735,-0.57735,-0.57735;2.0944rad)
  diameter = 4
  invert = false
  length = 2
  lengthCustom = 8
  matchOuter = false
  offset = 0
  thread = false
  type = 33
  expr: Placement = CommonBearingFixThrough_CommonBearingFixThrough001.Placement * CommonBearingFixThrough#HoleAxis_2.Placement * AttachmentOffset
FEATURE [Part::FeaturePython] Screw003  label="M3x8-Screw007"  # Fasteners workbench fastener (typed FeaturePython)
  AssemblyType = Asm4EE
  AttachedBy = Origin
  AttachedTo = Art23Optodisk_Art23Optodisk#HoleAxis_1
  AttachmentOffset = pos=(0,0,0) rot=(1,0,0;3.14159rad)
  Placement = pos=(-25,37,78) rot=(-1,0,0;1.5708rad)
  diameter = 4
  invert = false
  length = 2
  lengthCustom = 8
  matchOuter = false
  offset = 0
  thread = false
  type = 33
  expr: Placement = Art23Optodisk_Art23Optodisk.Placement * Art23Optodisk#HoleAxis_1.Placement * AttachmentOffset
FEATURE [Part::FeaturePython] Screw004  label="M3x8-Screw008"  # Fasteners workbench fastener (typed FeaturePython)
  AssemblyType = Asm4EE
  AttachedBy = Origin
  AttachedTo = Art23Optodisk_Art23Optodisk#HoleAxis_2
  AttachmentOffset = pos=(0,0,0) rot=(1,0,0;3.14159rad)
  Placement = pos=(25,37,78) rot=(-1,0,0;1.5708rad)
  diameter = 4
  invert = false
  length = 2
  lengthCustom = 8
  matchOuter = false
  offset = 0
  thread = false
  type = 33
  expr: Placement = Art23Optodisk_Art23Optodisk.Placement * Art23Optodisk#HoleAxis_2.Placement * AttachmentOffset
FEATURE [Part::FeaturePython] Screw005  label="M3x8-Screw011"  # Fasteners workbench fastener (typed FeaturePython)
  AssemblyType = Asm4EE
  AttachedBy = Origin
  AttachedTo = CommonBearingFixThrough_CommonBearingFixThrough#HoleAxis_2
  AttachmentOffset = pos=(0,0,0) rot=(1,0,0;3.14159rad)
  Placement = pos=(11,-50,81.5) rot=(1,0,0;1.5708rad)
  diameter = 4
  invert = false
  length = 2
  lengthCustom = 8
  matchOuter = false
  offset = 0
  thread = false
  type = 33
  expr: Placement = CommonBearingFixThrough_CommonBearingFixThrough.Placement * CommonBearingFixThrough#HoleAxis_2.Placement * AttachmentOffset
FEATURE [Part::FeaturePython] Screw006  label="M3x8-Screw012"  # Fasteners workbench fastener (typed FeaturePython)
  AssemblyType = Asm4EE
  AttachedBy = Origin
  AttachedTo = CommonBearingFixThrough_CommonBearingFixThrough#HoleAxis_1
  AttachmentOffset = pos=(0,0,0) rot=(1,0,0;3.14159rad)
  Placement = pos=(-11,-50,81.5) rot=(1,0,0;1.5708rad)
  diameter = 4
  invert = false
  length = 2
  lengthCustom = 8
  matchOuter = false
  offset = 0
  thread = false
  type = 33
  expr: Placement = CommonBearingFixThrough_CommonBearingFixThrough.Placement * CommonBearingFixThrough#HoleAxis_1.Placement * AttachmentOffset
FEATURE [Part::FeaturePython] Screw007  label="M3x25-Screw"  # Fasteners workbench fastener (typed FeaturePython)
  AssemblyType = Asm4EE
  AttachedBy = Origin
  AttachedTo = Art3Pulley_Art3Pulley#HoleAxis_1
  Placement = pos=(16,-50,68.5) rot=(1,0,0;1.5708rad)
  diameter = 4
  invert = false
  length = 8
  lengthCustom = 25
  matchOuter = false
  offset = 0
  thread = false
  type = 33
  expr: Placement = Art3Pulley_Art3Pulley.Placement * Art3Pulley#HoleAxis_1.Placement * AttachmentOffset
FEATURE [Part::FeaturePython] Screw008  label="M3x25-Screw003"  # Fasteners workbench fastener (typed FeaturePython)
  AssemblyType = Asm4EE
  AttachedBy = Origin
  AttachedTo = Art3Pulley_Art3Pulley#HoleAxis_4
  Placement = pos=(-2.9e-14,-50,99.5) rot=(1,0,0;1.5708rad)
  diameter = 4
  invert = false
  length = 8
  lengthCustom = 25
  matchOuter = false
  offset = 0
  thread = false
  type = 33
  expr: Placement = Art3Pulley_Art3Pulley.Placement * Art3Pulley#HoleAxis_4.Placement * AttachmentOffset
FEATURE [Part::FeaturePython] Screw009  label="M3x25-Screw004"  # Fasteners workbench fastener (typed FeaturePython)
  AssemblyType = Asm4EE
  AttachedBy = Origin
  AttachedTo = Art3Pulley_Art3Pulley#HoleAxis_2
  Placement = pos=(-16,-50,68.5) rot=(1,0,0;1.5708rad)
  diameter = 4
  invert = false
  length = 8
  lengthCustom = 25
  matchOuter = false
  offset = 0
  thread = false
  type = 33
  expr: Placement = Art3Pulley_Art3Pulley.Placement * Art3Pulley#HoleAxis_2.Placement * AttachmentOffset
FEATURE [Part::FeaturePython] Screw010  label="M3x16-Screw"  # Fasteners workbench fastener (typed FeaturePython)
  AssemblyType = Asm4EE
  AttachedBy = Origin
  AttachedTo = Art3Pulley_Art3Pulley#HoleAxis_3
  AttachmentOffset = pos=(0,0,10) rot=(0,0,1;0rad)
  Placement = pos=(-2.1e-14,-46.5,44.15) rot=(1,0,0;3.14159rad)
  diameter = 4
  invert = false
  length = 6
  lengthCustom = 16
  matchOuter = false
  offset = 0
  thread = false
  type = 33
  expr: Placement = Art3Pulley_Art3Pulley.Placement * Art3Pulley#HoleAxis_3.Placement * AttachmentOffset
FEATURE [Part::FeaturePython] Screw011  label="M3x12-Screw"  # Fasteners workbench fastener (typed FeaturePython)
  AssemblyType = Asm4EE
  AttachedBy = Origin
  AttachedTo = Art3Body_Art3Body#HoleAxis_2
  AttachmentOffset = pos=(0,0,0) rot=(1,0,0;3.14159rad)
  Placement = pos=(-48,-16,83) rot=(0.57735,0.57735,-0.57735;4.18879rad)
  diameter = 4
  invert = false
  length = 4
  lengthCustom = 12
  matchOuter = false
  offset = 0
  thread = false
  type = 33
  expr: Placement = Art3Body_Art3Body.Placement * Art3Body#HoleAxis_2.Placement * AttachmentOffset
FEATURE [Part::FeaturePython] Screw012  label="M3x12-Screw004"  # Fasteners workbench fastener (typed FeaturePython)
  AssemblyType = Asm4EE
  AttachedBy = Origin
  AttachedTo = Art3Body_Art3Body#HoleAxis_1
  AttachmentOffset = pos=(0,0,0) rot=(1,0,0;3.14159rad)
  Placement = pos=(-48,-16,115) rot=(0.57735,0.57735,-0.57735;4.18879rad)
  diameter = 4
  invert = false
  length = 4
  lengthCustom = 12
  matchOuter = false
  offset = 0
  thread = false
  type = 33
  expr: Placement = Art3Body_Art3Body.Placement * Art3Body#HoleAxis_1.Placement * AttachmentOffset
FEATURE [Part::FeaturePython] Screw013  label="M3x12-Screw005"  # Fasteners workbench fastener (typed FeaturePython)
  AssemblyType = Asm4EE
  AttachedBy = Origin
  AttachedTo = Art3Body_Art3Body#HoleAxis_4
  AttachmentOffset = pos=(0,0,0) rot=(1,0,0;3.14159rad)
  Placement = pos=(-48,16,83) rot=(0.57735,0.57735,-0.57735;4.18879rad)
  diameter = 4
  invert = false
  length = 4
  lengthCustom = 12
  matchOuter = false
  offset = 0
  thread = false
  type = 33
  expr: Placement = Art3Body_Art3Body.Placement * Art3Body#HoleAxis_4.Placement * AttachmentOffset
FEATURE [Part::FeaturePython] Screw014  label="M3x12-Screw006"  # Fasteners workbench fastener (typed FeaturePython)
  AssemblyType = Asm4EE
  AttachedBy = Origin
  AttachedTo = Art3Body_Art3Body#HoleAxis_3
  AttachmentOffset = pos=(0,0,0) rot=(1,0,0;3.14159rad)
  Placement = pos=(-48,16,115) rot=(0.57735,0.57735,-0.57735;4.18879rad)
  diameter = 4
  invert = false
  length = 4
  lengthCustom = 12
  matchOuter = false
  offset = 0
  thread = false
  type = 33
  expr: Placement = Art3Body_Art3Body.Placement * Art3Body#HoleAxis_3.Placement * AttachmentOffset
FEATURE [Part::FeaturePython] Screw015  label="M3x16-Screw005"  # Fasteners workbench fastener (typed FeaturePython)
  AssemblyType = Asm4EE
  AttachedBy = Origin
  AttachedTo = Art3Body_Art3Body#HoleAxis_18
  AttachmentOffset = pos=(0,0,0) rot=(1,0,0;3.14159rad)
  Placement = pos=(-22.5,-39,11) rot=(0,0,1;0rad)
  diameter = 4
  invert = false
  length = 6
  lengthCustom = 16
  matchOuter = false
  offset = 0
  thread = false
  type = 33
  expr: Placement = Art3Body_Art3Body.Placement * Art3Body#HoleAxis_18.Placement * AttachmentOffset
FEATURE [Part::FeaturePython] Screw016  label="M3x16-Screw006"  # Fasteners workbench fastener (typed FeaturePython)
  AssemblyType = Asm4EE
  AttachedBy = Origin
  AttachedTo = Art3Body_Art3Body#HoleAxis_17
  AttachmentOffset = pos=(0,0,0) rot=(1,0,0;3.14159rad)
  Placement = pos=(22.5,-39,11) rot=(0,0,1;0rad)
  diameter = 4
  invert = false
  length = 6
  lengthCustom = 16
  matchOuter = false
  offset = 0
  thread = false
  type = 33
  expr: Placement = Art3Body_Art3Body.Placement * Art3Body#HoleAxis_17.Placement * AttachmentOffset
FEATURE [Part::FeaturePython] Screw017  label="M3x16-Screw007"  # Fasteners workbench fastener (typed FeaturePython)
  AssemblyType = Asm4EE
  AttachedBy = Origin
  AttachedTo = Art3Body_Art3Body#HoleAxis_16
  AttachmentOffset = pos=(0,0,0) rot=(1,0,0;3.14159rad)
  Placement = pos=(-22.5,39,11) rot=(0,0,1;0rad)
  diameter = 4
  invert = false
  length = 6
  lengthCustom = 16
  matchOuter = false
  offset = 0
  thread = false
  type = 33
  expr: Placement = Art3Body_Art3Body.Placement * Art3Body#HoleAxis_16.Placement * AttachmentOffset
FEATURE [Part::FeaturePython] Screw018  label="M3x16-Screw008"  # Fasteners workbench fastener (typed FeaturePython)
  AssemblyType = Asm4EE
  AttachedBy = Origin
  AttachedTo = Art3Body_Art3Body#HoleAxis_15
  AttachmentOffset = pos=(0,0,0) rot=(1,0,0;3.14159rad)
  Placement = pos=(22.5,39,11) rot=(0,0,1;0rad)
  diameter = 4
  invert = false
  length = 6
  lengthCustom = 16
  matchOuter = false
  offset = 0
  thread = false
  type = 33
  expr: Placement = Art3Body_Art3Body.Placement * Art3Body#HoleAxis_15.Placement * AttachmentOffset
FEATURE [Part::FeaturePython] Screw019  label="M3x8-Screw017"  # Fasteners workbench fastener (typed FeaturePython)
  AssemblyType = Asm4EE
  AttachedBy = Origin
  AttachedTo = Art4MotorFix_Art4MotorFix#HoleAxis_5
  Placement = pos=(12.35,15.5,79.6) rot=(0,1,0;3.14159rad)
  diameter = 4
  invert = false
  length = 2
  lengthCustom = 8
  matchOuter = false
  offset = 0
  thread = false
  type = 33
  expr: Placement = Art4MotorFix_Art4MotorFix.Placement * Art4MotorFix#HoleAxis_5.Placement * AttachmentOffset
FEATURE [Part::FeaturePython] Screw020  label="M3x8-Screw018"  # Fasteners workbench fastener (typed FeaturePython)
  AssemblyType = Asm4EE
  AttachedBy = Origin
  AttachedTo = Art4MotorFix_Art4MotorFix#HoleAxis_6
  Placement = pos=(12.35,-15.5,79.6) rot=(0,1,0;3.14159rad)
  diameter = 4
  invert = false
  length = 2
  lengthCustom = 8
  matchOuter = false
  offset = 0
  thread = false
  type = 33
  expr: Placement = Art4MotorFix_Art4MotorFix.Placement * Art4MotorFix#HoleAxis_6.Placement * AttachmentOffset
FEATURE [Part::FeaturePython] Screw021  label="M3x8-Screw019"  # Fasteners workbench fastener (typed FeaturePython)
  AssemblyType = Asm4EE
  AttachedBy = Origin
  AttachedTo = Art4MotorFix_Art4MotorFix#HoleAxis_4
  Placement = pos=(43.35,15.5,79.6) rot=(0,1,0;3.14159rad)
  diameter = 4
  invert = false
  length = 2
  lengthCustom = 8
  matchOuter = false
  offset = 0
  thread = false
  type = 33
  expr: Placement = Art4MotorFix_Art4MotorFix.Placement * Art4MotorFix#HoleAxis_4.Placement * AttachmentOffset
FEATURE [Part::FeaturePython] Screw022  label="M3x8-Screw020"  # Fasteners workbench fastener (typed FeaturePython)
  AssemblyType = Asm4EE
  AttachedBy = Origin
  AttachedTo = Art4MotorFix_Art4MotorFix#HoleAxis_1
  Placement = pos=(43.35,-15.5,79.6) rot=(0,1,0;3.14159rad)
  diameter = 4
  invert = false
  length = 2
  lengthCustom = 8
  matchOuter = false
  offset = 0
  thread = false
  type = 33
  expr: Placement = Art4MotorFix_Art4MotorFix.Placement * Art4MotorFix#HoleAxis_1.Placement * AttachmentOffset
FEATURE [Part::FeaturePython] Screw023  label="M3x6-Screw"  # Fasteners workbench fastener (typed FeaturePython)
  AssemblyType = Asm4EE
  AttachedBy = Origin
  AttachedTo = Art3Body_Art3Body#HoleAxis_6
  AttachmentOffset = pos=(0,0,0) rot=(1,0,0;3.14159rad)
  Placement = pos=(51,4.5,77.6) rot=(0.57735,-0.57735,0.57735;4.18879rad)
  diameter = 4
  invert = false
  length = 1
  lengthCustom = 6
  matchOuter = false
  offset = 0
  thread = false
  type = 33
  expr: Placement = Art3Body_Art3Body.Placement * Art3Body#HoleAxis_6.Placement * AttachmentOffset
FEATURE [Part::FeaturePython] Screw024  label="M3x6-Screw001"  # Fasteners workbench fastener (typed FeaturePython)
  AssemblyType = Asm4EE
  AttachedBy = Origin
  AttachedTo = Art3Body_Art3Body#HoleAxis_5
  AttachmentOffset = pos=(0,0,0) rot=(1,0,0;3.14159rad)
  Placement = pos=(51,-4.5,77.6) rot=(0.57735,-0.57735,0.57735;4.18879rad)
  diameter = 4
  invert = false
  length = 1
  lengthCustom = 6
  matchOuter = false
  offset = 0
  thread = false
  type = 33
  expr: Placement = Art3Body_Art3Body.Placement * Art3Body#HoleAxis_5.Placement * AttachmentOffset
FEATURE [Part::FeaturePython] Screw025  label="M3x8-Screw021"  # Fasteners workbench fastener (typed FeaturePython)
  AssemblyType = Asm4EE
  AttachedBy = Origin
  AttachedTo = Art4MotorGear_Art4MotorGear#HoleAxis_1
  AttachmentOffset = pos=(0,0,0) rot=(1,0,0;3.14159rad)
  Placement = pos=(36.85,2.7e-14,71.1) rot=(0.57735,0.57735,0.57735;2.0944rad)
  diameter = 4
  invert = false
  length = 2
  lengthCustom = 8
  matchOuter = false
  offset = 0
  thread = false
  type = 33
  expr: Placement = Art4MotorGear_Art4MotorGear.Placement * Art4MotorGear#HoleAxis_1.Placement * AttachmentOffset
FEATURE [App::DocumentObjectGroup] Group003  label="Fasteners"
  Group = -> [Nut001,Nut002,Nut003,Nut,Nut004,Nut005,Nut006,Nut007,Nut008,Nut009,Nut010,Nut012,Nut011,Nut013,Nut014,Nut015,Nut016,Nut017,Nut018,Nut019,Nut020,Nut021,Screw001,Screw002,Screw003,Screw004,Screw006,Screw005,Screw008,Screw007,Screw009,Screw010,Screw011,Screw012,Screw013,Screw014,Screw015,Screw016,Screw017,Screw018,Screw019,Screw020,Screw021,Screw022,Screw023,Screw024,Screw,Screw025]
FEATURE [PartDesign::CoordinateSystem] LCS_Art2Fix
  AttacherType = Attacher::AttachEngine3D
  Placement = pos=(0,0,81.5) rot=(0,0,1;0rad)
FEATURE [PartDesign::CoordinateSystem] LCS_Art4Fix
  AttacherType = Attacher::AttachEngine3D
  Placement = pos=(0,0,-1) rot=(0,0,1;0rad)
FEATURE [App::Part] Model
  Configuration = 0
  Group = -> [LCS_Origin,Constraints,Variables,Art3Body_Art3Body,Art23Optodisk_Art23Optodisk,Art3Pulley_Art3Pulley,Art4MotorFix_Art4MotorFix,Stepper_Nema17x34001,Art4MotorGear_Art4MotorGear,Fan_40x40001,Bearing_625ZZ001,Bearing_625ZZ002,CommonBearingFixThrough_CommonBearingFixThrough,CommonBearingFixThrough_CommonBearingFixThrough001,OpticSensor,Art4BearingRing_Art4BearingRing,BearingBalls,LCS_Art2Fix,+50 more]
  Origin = -> Origin
  Type = Assembly4 Model
---- part AssemblyArt4.FCStd = doc fcstd_829bac75b840 (72356 chars; too large to inline — full recipe in that document) ----
---- part AssemblyArt56.FCStd = doc fcstd_7013da0a336a ----
FCSTD DOCUMENT  (FreeCAD 0.19R24276 (Git))
Label: AssemblyArt56
License: All rights reserved
LicenseURL: http://en.wikipedia.org/wiki/All_rights_reserved
objects: Part::FeaturePython×43, App::Link×20, PartDesign::CoordinateSystem×12, PartDesign::Line×8, App::DocumentObjectGroup×7, App::Part×6, Part::Feature×4, App::FeaturePython×1, Part::Part2DObjectPython×1, Part::Mirroring×1
note: 69 computed .brp shape members not serialized (recipe doc carries the construction recipe); baked Part::Feature solids carry a one-line shape summary decoded from their .brp
EXTERNAL_REF file=Art56MotorCoverRing.FCStd obj=LCS_Art56MotorCoverRing
EXTERNAL_REF file=Art56MotorCoverRing.FCStd obj=Body
EXTERNAL_REF file=Art56MotorCoverRing.FCStd obj=LCS_BearingFix
EXTERNAL_REF file=CommonBearingFixThrough.FCStd obj=LCS_CommonBearingFixThrough
EXTERNAL_REF file=CommonBearingFixThrough.FCStd obj=Body
EXTERNAL_REF file=Art56GearPlate.FCStd obj=LCS_Art56GearPlate
EXTERNAL_REF file=Art56MotorCoverRing.FCStd obj=LCS_BigGear
EXTERNAL_REF file=Art56GearPlate.FCStd obj=Body
EXTERNAL_REF file=Art56MotorCoverRing.FCStd obj=LCS_SmallGear2
EXTERNAL_REF file=Art56SmallGear.FCStd obj=LCS_Art56SmallGear
EXTERNAL_REF file=Art56SmallGear.FCStd obj=Body
EXTERNAL_REF file=Art56MotorCoverRing.FCStd obj=LCS_SmallGear1
EXTERNAL_REF file=Art56GearPlate.FCStd obj=LCS_Bearing
EXTERNAL_REF file=Art56MotorCoverRing.FCStd obj=LCS_Bearing
EXTERNAL_REF file=Art56SmallGear.FCStd obj=LCS_Pulley
EXTERNAL_REF file=Art56GearPlate.FCStd obj=HoleAxis_2
EXTERNAL_REF file=Art56MotorCoverRing.FCStd obj=HoleAxis_2
EXTERNAL_REF file=Art56MotorCoverRing.FCStd obj=HoleAxis_1
EXTERNAL_REF file=Art56GearPlate.FCStd obj=HoleAxis_1
EXTERNAL_REF file=Art56GearPlate.FCStd obj=HoleAxis_3
EXTERNAL_REF file=Art56SmallGear.FCStd obj=HoleAxis_1
EXTERNAL_REF file=CommonBearingFixThrough.FCStd obj=HoleAxis_1
EXTERNAL_REF file=CommonBearingFixThrough.FCStd obj=HoleAxis_2
EXTERNAL_REF file=Art56MotorCoverRing.FCStd obj=HoleAxis_3
EXTERNAL_REF file=Art56GearPlate.FCStd obj=LCS_Gripper
EXTERNAL_REF file=GripperBot.FCStd obj=LCS_GripperBot
EXTERNAL_REF file=GripperBot.FCStd obj=Body
EXTERNAL_REF file=GripperBot.FCStd obj=LCS_GripperTop
EXTERNAL_REF file=GripperTop.FCStd obj=LCS_GripperTop
EXTERNAL_REF file=GripperTop.FCStd obj=Body
EXTERNAL_REF file=GripperBot.FCStd obj=LCS_Servomotor
EXTERNAL_REF file=GripperActiveArm.FCStd obj=LCS_GripperActiveArm
EXTERNAL_REF file=GripperActiveArm.FCStd obj=Body
EXTERNAL_REF file=GripperBot.FCStd obj=LCS_PassiveArm
EXTERNAL_REF file=GripperPassiveArm.FCStd obj=LCS_GripperPassiveArm
EXTERNAL_REF file=GripperPassiveArm.FCStd obj=Body
EXTERNAL_REF file=GripperArm.FCStd obj=LCS_GripperArm
EXTERNAL_REF file=GripperBot.FCStd obj=LCS_Arm1
EXTERNAL_REF file=GripperArm.FCStd obj=Body
EXTERNAL_REF file=GripperBot.FCStd obj=LCS_Arm2
EXTERNAL_REF file=GripperBot.FCStd obj=HoleAxis_9
EXTERNAL_REF file=GripperBot.FCStd obj=HoleAxis_8
EXTERNAL_REF file=GripperBot.FCStd obj=HoleAxis_3
EXTERNAL_REF file=GripperBot.FCStd obj=HoleAxis_4
EXTERNAL_REF file=GripperBot.FCStd obj=HoleAxis_6
EXTERNAL_REF file=GripperBot.FCStd obj=HoleAxis_7
EXTERNAL_REF file=GripperBot.FCStd obj=HoleAxis_11
EXTERNAL_REF file=GripperBot.FCStd obj=HoleAxis_10
EXTERNAL_REF file=GripperBot.FCStd obj=HoleAxis_5
EXTERNAL_REF file=GripperTop.FCStd obj=HoleAxis_5
EXTERNAL_REF file=GripperTop.FCStd obj=HoleAxis_6
EXTERNAL_REF file=GripperTop.FCStd obj=HoleAxis_2
EXTERNAL_REF file=GripperTop.FCStd obj=HoleAxis_3
EXTERNAL_REF file=GripperTop.FCStd obj=HoleAxis_4
EXTERNAL_REF file=GripperTop.FCStd obj=HoleAxis_1
EXTERNAL_REF file=GripperBot.FCStd obj=HoleAxis_1
EXTERNAL_REF file=GripperBot.FCStd obj=HoleAxis_2
EXTERNAL_REF file=GripperArm.FCStd obj=LCS_GripperArm_1
EXTERNAL_REF file=GripperFinger.FCStd obj=LCS_GripperFinger
EXTERNAL_REF file=GripperFinger.FCStd obj=Body
EXTERNAL_REF file=GripperFinger.FCStd obj=HoleAxis_3
EXTERNAL_REF file=GripperFinger.FCStd obj=HoleAxis_4
EXTERNAL_REF file=GripperFinger.FCStd obj=HoleAxis_1
EXTERNAL_REF file=GripperFinger.FCStd obj=HoleAxis_2
EXTERNAL_REF file=GripperActiveArm.FCStd obj=HoleAxis_3
EXTERNAL_REF file=GripperActiveArm.FCStd obj=HoleAxis_2
EXTERNAL_REF file=GripperActiveArm.FCStd obj=HoleAxis_1

FEATURE [PartDesign::CoordinateSystem] LCS_Origin
  AttacherType = Attacher::AttachEngine3D
  MapMode = 2
  Support = -> [X_Axis]
FEATURE [App::DocumentObjectGroup] Constraints
FEATURE [App::FeaturePython] Variables  # WARN: FeaturePython — macro-defined, semantics opaque (R4)
FEATURE [App::Link] Art56MotorCoverRing_Art56MotorCoverRing
  AssemblyType = Asm4EE
  AttachedBy = #LCS_Art56MotorCoverRing
  AttachedTo = Parent Assembly#LCS_Origin
  AttachmentOffset = pos=(0,0,0) rot=(0,1,0;4.71239rad)
  LinkPlacement = pos=(0,0,0) rot=(0.57735,-0.57735,0.57735;4.18879rad)
  LinkedObject = -> <external Art56MotorCoverRing.FCStd>#Body
  Placement = pos=(0,0,0) rot=(0.57735,-0.57735,0.57735;4.18879rad)
  expr: Placement = LCS_Origin.Placement * AttachmentOffset * Art56MotorCoverRing#LCS_Art56MotorCoverRing.Placement ^ -1
FEATURE [App::Link] CommonBearingFixThrough_CommonBearingFixThrough
  AssemblyType = Asm4EE
  AttachedBy = #LCS_CommonBearingFixThrough
  AttachedTo = Art56MotorCoverRing_Art56MotorCoverRing#LCS_BearingFix
  AttachmentOffset = pos=(0,0,0) rot=(1,0,0;3.14159rad)
  LinkPlacement = pos=(-3,-1.88e-14,-8e-16) rot=(-0.57735,-0.57735,0.57735;2.0944rad)
  LinkedObject = -> <external CommonBearingFixThrough.FCStd>#Body
  Placement = pos=(-3,-1.88e-14,-8e-16) rot=(-0.57735,-0.57735,0.57735;2.0944rad)
  expr: Placement = Art56MotorCoverRing_Art56MotorCoverRing.Placement * Art56MotorCoverRing#LCS_BearingFix.Placement * AttachmentOffset * CommonBearingFixThrough#LCS_CommonBearingFixThrough.Placement ^ -1
FEATURE [App::Link] Art56GearPlate_Art56GearPlate
  AssemblyType = Asm4EE
  AttachedBy = #LCS_Art56GearPlate
  AttachedTo = Art56MotorCoverRing_Art56MotorCoverRing#LCS_BigGear
  AttachmentOffset = pos=(0,0,0) rot=(0.258819,-0.965926,0;3.14159rad)
  LinkPlacement = pos=(-1.06e-14,1.1e-15,21.5) rot=(-0.866025,0.5,0;3.14159rad)
  LinkedObject = -> <external Art56GearPlate.FCStd>#Body
  Placement = pos=(-1.06e-14,1.1e-15,21.5) rot=(-0.866025,0.5,0;3.14159rad)
  expr: Placement = Art56MotorCoverRing_Art56MotorCoverRing.Placement * Art56MotorCoverRing#LCS_BigGear.Placement * AttachmentOffset * Art56GearPlate#LCS_Art56GearPlate.Placement ^ -1
FEATURE [App::Link] Art56SmallGear_Art56SmallGear
  AssemblyType = Asm4EE
  AttachedBy = #LCS_Art56SmallGear
  AttachedTo = Art56MotorCoverRing_Art56MotorCoverRing#LCS_SmallGear2
  AttachmentOffset = pos=(0,0,0) rot=(0.113203,-0.993572,0;3.14159rad)
  LinkPlacement = pos=(-39.4,6.86696e-05,-1.58536e-05) rot=(-0.616308,0.490234,-0.616308;2.22999rad)
  LinkedObject = -> <external Art56SmallGear.FCStd>#Body
  Placement = pos=(-39.4,6.86696e-05,-1.58536e-05) rot=(-0.616308,0.490234,-0.616308;2.22999rad)
  expr: Placement = Art56MotorCoverRing_Art56MotorCoverRing.Placement * Art56MotorCoverRing#LCS_SmallGear2.Placement * AttachmentOffset * Art56SmallGear#LCS_Art56SmallGear.Placement ^ -1
FEATURE [App::Link] Art56SmallGear_Art56SmallGear001
  AssemblyType = Asm4EE
  AttachedBy = #LCS_Art56SmallGear
  AttachedTo = Art56MotorCoverRing_Art56MotorCoverRing#LCS_SmallGear1
  LinkPlacement = pos=(39.4,7.04758e-05,1.76e-14) rot=(-0.57735,0.57735,0.57735;4.18879rad)
  LinkedObject = -> <external Art56SmallGear.FCStd>#Body
  Placement = pos=(39.4,7.04758e-05,1.76e-14) rot=(-0.57735,0.57735,0.57735;4.18879rad)
  expr: Placement = Art56MotorCoverRing_Art56MotorCoverRing.Placement * Art56MotorCoverRing#LCS_SmallGear1.Placement * AttachmentOffset * Art56SmallGear#LCS_Art56SmallGear.Placement ^ -1
FEATURE [PartDesign::CoordinateSystem] LCS_0
  AttacherType = Attacher::AttachEngine3D
  MapMode = 2
  Support = -> [X_Axis003]
FEATURE [Part::Feature] Compound001  label="Bearing 625ZZ"
  shape: bbox 16 x 16 x 5 mm, 86 faces, 3 solids (baked)
FEATURE [App::Part] Bearing_625ZZ
  Group = -> [LCS_0,Compound001]
  Origin = -> Origin003
FEATURE [App::DocumentObjectGroup] Group002  label="Bearing"
  Group = -> [Bearing_625ZZ]
FEATURE [App::Link] Bearing_625ZZ001
  AssemblyType = Asm4EE
  AttachedBy = #LCS_0
  AttachedTo = Art56GearPlate_Art56GearPlate#LCS_Bearing
  LinkPlacement = pos=(-9.1e-15,2e-15,21.5) rot=(0,0,-1;1.0472rad)
  LinkedObject = -> Bearing_625ZZ
  Placement = pos=(-9.1e-15,2e-15,21.5) rot=(0,0,-1;1.0472rad)
  expr: Placement = Art56GearPlate_Art56GearPlate.Placement * Art56GearPlate#LCS_Bearing.Placement * AttachmentOffset * LCS_0.Placement ^ -1
FEATURE [App::Link] Bearing_625ZZ002
  AssemblyType = Asm4EE
  AttachedBy = #LCS_0
  AttachedTo = Art56MotorCoverRing_Art56MotorCoverRing#LCS_Bearing
  LinkPlacement = pos=(2,6e-16,1e-15) rot=(-0.685101,-0.247533,0.685101;2.65628rad)
  LinkedObject = -> Bearing_625ZZ
  Placement = pos=(2,6e-16,1e-15) rot=(-0.685101,-0.247533,0.685101;2.65628rad)
  expr: Placement = Art56MotorCoverRing_Art56MotorCoverRing.Placement * Art56MotorCoverRing#LCS_Bearing.Placement * AttachmentOffset * LCS_0.Placement ^ -1
FEATURE [Part::Feature] Cut002004  label="GT2x40Pulley"
  shape: bbox 28 x 28 x 15 mm, 94 faces (baked)
FEATURE [PartDesign::CoordinateSystem] LCS_Pulley_GT2x40
  AttacherType = Attacher::AttachEngine3D
  MapMode = 11
  Placement = pos=(0,0,15) rot=(0,0,1;1.5708rad)
  Support = -> [Cut002004]
FEATURE [App::Part] Pulley_GT2x40
  Group = -> [Cut002004,LCS_Pulley_GT2x40]
  Origin = -> Origin004
FEATURE [App::DocumentObjectGroup] Group  label="Pulleys"
  Group = -> [Pulley_GT2x40]
FEATURE [App::Link] Pulley_GT2x40001
  AssemblyType = Asm4EE
  AttachedBy = #LCS_Pulley_GT2x40
  AttachedTo = Art56SmallGear_Art56SmallGear#LCS_Pulley
  AttachmentOffset = pos=(0,0,0) rot=(0.803857,-0.594823,0;3.14159rad)
  LinkPlacement = pos=(-18,6.86696e-05,-1.58536e-05) rot=(0.706891,0.024685,-0.706891;3.19095rad)
  LinkedObject = -> Pulley_GT2x40
  Placement = pos=(-18,6.86696e-05,-1.58536e-05) rot=(0.706891,0.024685,-0.706891;3.19095rad)
  expr: Placement = Art56SmallGear_Art56SmallGear.Placement * Art56SmallGear#LCS_Pulley.Placement * AttachmentOffset * LCS_Pulley_GT2x40.Placement ^ -1
FEATURE [App::Link] Pulley_GT2x40002
  AssemblyType = Asm4EE
  AttachedBy = #LCS_Pulley_GT2x40
  AttachedTo = Art56SmallGear_Art56SmallGear001#LCS_Pulley
  AttachmentOffset = pos=(0,0,0) rot=(0.803857,-0.594823,0;3.14159rad)
  LinkPlacement = pos=(18,7.04758e-05,1.17e-14) rot=(-0.703191,-0.105093,-0.703191;3.35101rad)
  LinkedObject = -> Pulley_GT2x40
  Placement = pos=(18,7.04758e-05,1.17e-14) rot=(-0.703191,-0.105093,-0.703191;3.35101rad)
  expr: Placement = Art56SmallGear_Art56SmallGear001.Placement * Art56SmallGear#LCS_Pulley.Placement * AttachmentOffset * LCS_Pulley_GT2x40.Placement ^ -1
FEATURE [Part::FeaturePython] Nut  label="M3-Nut"  # Fasteners workbench fastener (typed FeaturePython)
  AssemblyType = Asm4EE
  AttachedBy = Origin
  AttachedTo = Art56GearPlate_Art56GearPlate#HoleAxis_2
  AttachmentOffset = pos=(0,0,0) rot=(0,0,1;1.5708rad)
  Placement = pos=(-10.8253,-6.25,59.5) rot=(-0.250563,0.935113,0.250563;1.63783rad)
  diameter = 4
  invert = false
  matchOuter = false
  offset = 0
  thread = false
  type = 7
  expr: Placement = Art56GearPlate_Art56GearPlate.Placement * Art56GearPlate#HoleAxis_2.Placement * AttachmentOffset
FEATURE [Part::FeaturePython] Nut001  label="M3-Nut019"  # Fasteners workbench fastener (typed FeaturePython)
  AssemblyType = Asm4EE
  AttachedBy = Origin
  AttachedTo = Art56MotorCoverRing_Art56MotorCoverRing#HoleAxis_2
  AttachmentOffset = pos=(0,0,0) rot=(0.707107,-0.707107,0;3.14159rad)
  Placement = pos=(-3e-15,11,-3e-15) rot=(0,1,0;1.5708rad)
  diameter = 4
  invert = false
  matchOuter = false
  offset = 0
  thread = false
  type = 7
  expr: Placement = Art56MotorCoverRing_Art56MotorCoverRing.Placement * Art56MotorCoverRing#HoleAxis_2.Placement * AttachmentOffset
FEATURE [Part::FeaturePython] Nut002  label="M3-Nut018"  # Fasteners workbench fastener (typed FeaturePython)
  AssemblyType = Asm4EE
  AttachedBy = Origin
  AttachedTo = Art56MotorCoverRing_Art56MotorCoverRing#HoleAxis_1
  AttachmentOffset = pos=(0,0,0) rot=(0.707107,-0.707107,0;3.14159rad)
  Placement = pos=(0,-11,3e-15) rot=(0,1,0;1.5708rad)
  diameter = 4
  invert = false
  matchOuter = false
  offset = 0
  thread = false
  type = 7
  expr: Placement = Art56MotorCoverRing_Art56MotorCoverRing.Placement * Art56MotorCoverRing#HoleAxis_1.Placement * AttachmentOffset
FEATURE [Part::FeaturePython] Nut003  label="M3-Nut218"  # Fasteners workbench fastener (typed FeaturePython)
  AssemblyType = Asm4EE
  AttachedBy = Origin
  AttachedTo = Art56GearPlate_Art56GearPlate#HoleAxis_1
  AttachmentOffset = pos=(0,0,0) rot=(0,0,1;1.5708rad)
  Placement = pos=(10.8253,-6.25,59.5) rot=(-0.694747,0.186157,0.694747;2.77349rad)
  diameter = 4
  invert = false
  matchOuter = false
  offset = 0
  thread = false
  type = 7
  expr: Placement = Art56GearPlate_Art56GearPlate.Placement * Art56GearPlate#HoleAxis_1.Placement * AttachmentOffset
FEATURE [Part::FeaturePython] Nut004  label="M3-Nut219"  # Fasteners workbench fastener (typed FeaturePython)
  AssemblyType = Asm4EE
  AttachedBy = Origin
  AttachedTo = Art56GearPlate_Art56GearPlate#HoleAxis_3
  AttachmentOffset = pos=(0,0,0) rot=(0,0,1;1.5708rad)
  Placement = pos=(2.3e-14,12.5,59.5) rot=(0.57735,0.57735,-0.57735;2.0944rad)
  diameter = 4
  invert = false
  matchOuter = false
  offset = 0
  thread = false
  type = 7
  expr: Placement = Art56GearPlate_Art56GearPlate.Placement * Art56GearPlate#HoleAxis_3.Placement * AttachmentOffset
FEATURE [Part::FeaturePython] Screw  label="M5x16-Screw"  # Fasteners workbench fastener (typed FeaturePython)
  AssemblyType = Asm4EE
  AttachedBy = Origin
  AttachedTo = Art56GearPlate_Art56GearPlate#LCS_Bearing
  AttachmentOffset = pos=(0,0,5) rot=(0,0,1;0rad)
  Placement = pos=(-1e-14,2e-15,26.5) rot=(0,0,-1;1.0472rad)
  diameter = 6
  invert = false
  length = 4
  lengthCustom = 16
  matchOuter = false
  offset = 0
  thread = false
  type = 33
  expr: Placement = Art56GearPlate_Art56GearPlate.Placement * Art56GearPlate#LCS_Bearing.Placement * AttachmentOffset
FEATURE [Part::FeaturePython] Screw001  label="M3x6-Screw"  # Fasteners workbench fastener (typed FeaturePython)
  AssemblyType = Asm4EE
  AttachedBy = Origin
  AttachedTo = Art56SmallGear_Art56SmallGear#HoleAxis_1
  AttachmentOffset = pos=(0,0,0) rot=(1,0,0;3.14159rad)
  Placement = pos=(-30.25,0.76739,-10.9732) rot=(0.706891,-0.706891,-0.024685;3.19095rad)
  diameter = 4
  invert = false
  length = 1
  lengthCustom = 6
  matchOuter = false
  offset = 0
  thread = false
  type = 33
  expr: Placement = Art56SmallGear_Art56SmallGear.Placement * Art56SmallGear#HoleAxis_1.Placement * AttachmentOffset
FEATURE [Part::FeaturePython] Screw002  label="M3x8-Screw"  # Fasteners workbench fastener (typed FeaturePython)
  AssemblyType = Asm4EE
  AttachedBy = Origin
  AttachedTo = CommonBearingFixThrough_CommonBearingFixThrough#HoleAxis_1
  AttachmentOffset = pos=(0,0,0) rot=(1,0,0;3.14159rad)
  Placement = pos=(-4,-11,2e-15) rot=(0.57735,0.57735,-0.57735;4.18879rad)
  diameter = 4
  invert = false
  length = 2
  lengthCustom = 8
  matchOuter = false
  offset = 0
  thread = false
  type = 33
  expr: Placement = CommonBearingFixThrough_CommonBearingFixThrough.Placement * CommonBearingFixThrough#HoleAxis_1.Placement * AttachmentOffset
FEATURE [Part::FeaturePython] Screw003  label="M3x8-Screw001"  # Fasteners workbench fastener (typed FeaturePython)
  AssemblyType = Asm4EE
  AttachedBy = Origin
  AttachedTo = CommonBearingFixThrough_CommonBearingFixThrough#HoleAxis_2
  AttachmentOffset = pos=(0,0,0) rot=(1,0,0;3.14159rad)
  Placement = pos=(-4,11,-4e-15) rot=(0.57735,0.57735,-0.57735;4.18879rad)
  diameter = 4
  invert = false
  length = 2
  lengthCustom = 8
  matchOuter = false
  offset = 0
  thread = false
  type = 33
  expr: Placement = CommonBearingFixThrough_CommonBearingFixThrough.Placement * CommonBearingFixThrough#HoleAxis_2.Placement * AttachmentOffset
FEATURE [Part::FeaturePython] Screw004  label="M3x6-Screw001"  # Fasteners workbench fastener (typed FeaturePython)
  AssemblyType = Asm4EE
  AttachedBy = Origin
  AttachedTo = Art56SmallGear_Art56SmallGear001#HoleAxis_1
  AttachmentOffset = pos=(0,0,0) rot=(1,0,0;3.14159rad)
  Placement = pos=(30.25,3.21616,10.5194) rot=(-0.146221,-0.146221,-0.978386;1.59265rad)
  diameter = 4
  invert = false
  length = 1
  lengthCustom = 6
  matchOuter = false
  offset = 0
  thread = false
  type = 33
  expr: Placement = Art56SmallGear_Art56SmallGear001.Placement * Art56SmallGear#HoleAxis_1.Placement * AttachmentOffset
FEATURE [Part::FeaturePython] Nut005  label="M5-Nut"  # Fasteners workbench fastener (typed FeaturePython)
  AssemblyType = Asm4EE
  AttachedBy = Origin
  AttachedTo = Art56MotorCoverRing_Art56MotorCoverRing#HoleAxis_3
  AttachmentOffset = pos=(0,0,0) rot=(1,0,0;3.14159rad)
  Placement = pos=(-4e-15,4e-15,14) rot=(0.707107,-0.707107,0;3.14159rad)
  diameter = 3
  invert = false
  matchOuter = false
  offset = 0
  thread = false
  type = 5
  expr: Placement = Art56MotorCoverRing_Art56MotorCoverRing.Placement * Art56MotorCoverRing#HoleAxis_3.Placement * AttachmentOffset
FEATURE [PartDesign::CoordinateSystem] LCS_Art4Fix
  AttacherType = Attacher::AttachEngine3D
FEATURE [PartDesign::CoordinateSystem] LCS_0001
  AttacherType = Attacher::AttachEngine3D
  MapMode = 2
  Support = -> [X_Axis005]
FEATURE [Part::Feature] Compound002  label="Servomotor001"
  shape: bbox 19.8 x 54.6 x 44.5 mm, 458 faces, 8 solids (baked)
FEATURE [PartDesign::Line] HoleAxis_1
  AttacherType = Attacher::AttachEngineLine
  Length = 5.94263
  MapMode = 19
  Placement = pos=(9,-16.4104,-12.15) rot=(0,0,1;2.17509rad)
  ResizeMode = 1
  Support = -> [Compound002]
FEATURE [PartDesign::Line] HoleAxis_2
  AttacherType = Attacher::AttachEngineLine
  Length = 4.57317
  MapMode = 19
  Placement = pos=(-1,-16.4104,-12.15) rot=(-0.885489,-0.46466,0;3.14159rad)
  ResizeMode = 1
  Support = -> [Compound002]
FEATURE [PartDesign::Line] HoleAxis_3
  AttacherType = Attacher::AttachEngineLine
  Length = 5.94263
  MapMode = 19
  Placement = pos=(9,-66.1896,-12.15) rot=(-0.46466,0.885489,0;3.14159rad)
  ResizeMode = 1
  Support = -> [Compound002]
FEATURE [PartDesign::Line] HoleAxis_4
  AttacherType = Attacher::AttachEngineLine
  Length = 5.94263
  MapMode = 19
  Placement = pos=(-1,-66.1896,-12.15) rot=(0,0,-1;0.966502rad)
  ResizeMode = 1
  Support = -> [Compound002]
FEATURE [Part::Feature] Clone041003009009001  label="WheelHorn"
  shape: bbox 21 x 21 x 5.5 mm, 20 faces (baked)
FEATURE [PartDesign::CoordinateSystem] LCS_0002
  AttacherType = Attacher::AttachEngine3D
  MapMode = 2
  Support = -> [X_Axis006]
FEATURE [PartDesign::CoordinateSystem] LCS_ServomotorWheelHorn
  AttacherType = Attacher::AttachEngine3D
  MapMode = 11
  Placement = pos=(0,0,2.3) rot=(0,0,1;1.5708rad)
  Support = -> [Clone041003009009001]
FEATURE [PartDesign::CoordinateSystem] LCS_ActiveArm
  AttacherType = Attacher::AttachEngine3D
  MapMode = 45
  Support = -> [Clone041003009009001]
FEATURE [App::Part] ServomotorWheelHorn
  Group = -> [LCS_0002,Clone041003009009001,LCS_ServomotorWheelHorn,LCS_ActiveArm]
  Origin = -> Origin006
FEATURE [App::Link] GripperBot_GripperBot
  AssemblyType = Asm4EE
  AttachedBy = #LCS_GripperBot
  AttachedTo = Art56GearPlate_Art56GearPlate#LCS_Gripper
  AttachmentOffset = pos=(0,0,1) rot=(0.984808,-0.173648,0;3.14159rad)
  LinkPlacement = pos=(0.0466674,-17.1499,56.5) rot=(0.000962,-0.707106,-0.707106;3.13967rad)
  LinkedObject = -> <external GripperBot.FCStd>#Body
  Placement = pos=(0.0466674,-17.1499,56.5) rot=(0.000962,-0.707106,-0.707106;3.13967rad)
  expr: Placement = Art56GearPlate_Art56GearPlate.Placement * Art56GearPlate#LCS_Gripper.Placement * AttachmentOffset * GripperBot#LCS_GripperBot.Placement ^ -1
FEATURE [App::Link] Unnamed_GripperTop
  AssemblyType = Asm4EE
  AttachedBy = #LCS_GripperTop
  AttachedTo = GripperBot_GripperBot#LCS_GripperTop
  LinkPlacement = pos=(-0.007211,2.64999,56.5) rot=(0.000962,-0.707106,-0.707106;3.13967rad)
  LinkedObject = -> <external GripperTop.FCStd>#Body
  Placement = pos=(-0.007211,2.64999,56.5) rot=(0.000962,-0.707106,-0.707106;3.13967rad)
  expr: Placement = GripperBot_GripperBot.Placement * GripperBot#LCS_GripperTop.Placement * AttachmentOffset * GripperTop#LCS_GripperTop.Placement ^ -1
FEATURE [Part::Part2DObjectPython] Wire  # Draft 2D object (typed FeaturePython)
  Area = 0
  ChamferSize = 0
  Closed = true
  End = (9,-16.4104,-9.35)
  FilletRadius = 0
  Length = 119.558
  MakeFace = false
  Placement = pos=(9,-66.1896,-9.35) rot=(0,0,1;0rad)
  Points = (4) [(0,0,0),(-10,0,0),(-10,49.7792,0),(1.77636e-15,49.7792,0)]
  Start = (9,-66.1896,-9.35)
  Subdivisions = 0
FEATURE [PartDesign::CoordinateSystem] LCS_WheelHorn
  AttacherType = Attacher::AttachEngine3D
  MapMode = 11
  Placement = pos=(4,-31,5.35) rot=(0,0,1;3.13671rad)
  Support = -> [Compound002]
FEATURE [PartDesign::CoordinateSystem] LCS_Servomotor
  AttacherType = Attacher::AttachEngine3D
  MapMode = 45
  Placement = pos=(4,-41.3,-9.35) rot=(0,0,1;0rad)
  Support = -> [Wire]
FEATURE [App::Part] Servomotor
  Group = -> [LCS_0001,Compound002,HoleAxis_1,HoleAxis_2,HoleAxis_3,HoleAxis_4,LCS_WheelHorn,Wire,LCS_Servomotor]
  Origin = -> Origin005
FEATURE [App::DocumentObjectGroup] Group004  label="Electronics"
  Group = -> [Servomotor,ServomotorWheelHorn]
FEATURE [App::Link] Servomotor001  label="Servomotor002"
  AssemblyType = Asm4EE
  AttachedBy = #LCS_Servomotor
  AttachedTo = GripperBot_GripperBot#LCS_Servomotor
  LinkPlacement = pos=(45.5361,-7.67612,85) rot=(-0.576826,-0.578398,-0.576826;2.09282rad)
  LinkedObject = -> Servomotor
  Placement = pos=(45.5361,-7.67612,85) rot=(-0.576826,-0.578398,-0.576826;2.09282rad)
  expr: Placement = GripperBot_GripperBot.Placement * GripperBot#LCS_Servomotor.Placement * AttachmentOffset * LCS_Servomotor.Placement ^ -1
FEATURE [App::Link] ServomotorWheelHorn001
  AssemblyType = Asm4EE
  AttachedBy = #LCS_ServomotorWheelHorn
  AttachedTo = Servomotor001#LCS_WheelHorn
  AttachmentOffset = pos=(0,0,0) rot=(1,0,0;3.14159rad)
  LinkPlacement = pos=(14.5154,-0.110502,89) rot=(0.000763,0.707109,-0.707104;3.13622rad)
  LinkedObject = -> ServomotorWheelHorn
  Placement = pos=(14.5154,-0.110502,89) rot=(0.000763,0.707109,-0.707104;3.13622rad)
  expr: Placement = Servomotor001.Placement * LCS_WheelHorn.Placement * AttachmentOffset * LCS_ServomotorWheelHorn.Placement ^ -1
FEATURE [App::Link] GripperActiveArm_GripperActiveArm
  AssemblyType = Asm4EE
  AttachedBy = #LCS_GripperActiveArm
  AttachedTo = ServomotorWheelHorn001#LCS_ActiveArm
  AttachmentOffset = pos=(0,0,0) rot=(0,-1,0;3.14159rad)
  LinkPlacement = pos=(14.5216,-2.41049,89) rot=(-0.999992,-0.003801,-0.00108;1.5708rad)
  LinkedObject = -> <external GripperActiveArm.FCStd>#Body
  Placement = pos=(14.5216,-2.41049,89) rot=(-0.999992,-0.003801,-0.00108;1.5708rad)
  expr: Placement = ServomotorWheelHorn001.Placement * LCS_ActiveArm.Placement * AttachmentOffset * GripperActiveArm#LCS_GripperActiveArm.Placement ^ -1
FEATURE [App::Link] Unnamed3_GripperPassiveArm
  AssemblyType = Asm4EE
  AttachedBy = #LCS_GripperPassiveArm
  AttachedTo = GripperBot_GripperBot#LCS_PassiveArm
  AttachmentOffset = pos=(0,0,0) rot=(0,0,1;6.16538rad)
  LinkPlacement = pos=(-14.4927,-2.68945,89) rot=(-0.042624,0.706407,0.706521;3.06024rad)
  LinkedObject = -> <external GripperPassiveArm.FCStd>#Body
  Placement = pos=(-14.4927,-2.68945,89) rot=(-0.042624,0.706407,0.706521;3.06024rad)
  expr: Placement = GripperBot_GripperBot.Placement * GripperBot#LCS_PassiveArm.Placement * AttachmentOffset * GripperPassiveArm#LCS_GripperPassiveArm.Placement ^ -1
FEATURE [App::Link] Unnamed2_GripperArm
  AssemblyType = Asm4EE
  AttachedBy = #LCS_GripperArm
  AttachedTo = GripperBot_GripperBot#LCS_Arm1
  AttachmentOffset = pos=(0,0,0) rot=(0.707107,-0.707107,0;3.14159rad)
  LinkPlacement = pos=(-5.99277,-2.66632,107.5) rot=(-0.577873,0.576303,0.577873;2.09597rad)
  LinkedObject = -> <external GripperArm.FCStd>#Body
  Placement = pos=(-5.99277,-2.66632,107.5) rot=(-0.577873,0.576303,0.577873;2.09597rad)
  expr: Placement = GripperBot_GripperBot.Placement * GripperBot#LCS_Arm1.Placement * AttachmentOffset * GripperArm#LCS_GripperArm.Placement ^ -1
FEATURE [App::Link] Unnamed2_GripperArm001
  AssemblyType = Asm4EE
  AttachedBy = #LCS_GripperArm
  AttachedTo = GripperBot_GripperBot#LCS_Arm2
  AttachmentOffset = pos=(0,0,0) rot=(-0.707107,-0.707107,0;3.14159rad)
  LinkPlacement = pos=(6.00719,-2.63366,107.5) rot=(0.576826,0.578398,0.576826;4.19036rad)
  LinkedObject = -> <external GripperArm.FCStd>#Body
  Placement = pos=(6.00719,-2.63366,107.5) rot=(0.576826,0.578398,0.576826;4.19036rad)
  expr: Placement = GripperBot_GripperBot.Placement * GripperBot#LCS_Arm2.Placement * AttachmentOffset * GripperArm#LCS_GripperArm.Placement ^ -1
FEATURE [Part::FeaturePython] Nut011  label="M3-Nut213"  # Fasteners workbench fastener (typed FeaturePython)
  AssemblyType = Asm4EE
  AttachedBy = Origin
  AttachedTo = GripperBot_GripperBot#HoleAxis_9
  Placement = pos=(6.03032,-11.1336,107.5) rot=(-0.000962,0.707106,-0.707106;3.13967rad)
  diameter = 1
  invert = false
  matchOuter = false
  offset = 0
  thread = false
  type = 5
  expr: Placement = GripperBot_GripperBot.Placement * GripperBot#HoleAxis_9.Placement * AttachmentOffset
FEATURE [Part::FeaturePython] Nut012  label="M3-Nut215"  # Fasteners workbench fastener (typed FeaturePython)
  AssemblyType = Asm4EE
  AttachedBy = Origin
  AttachedTo = GripperBot_GripperBot#HoleAxis_8
  Placement = pos=(-5.96964,-11.1663,107.5) rot=(-0.000962,0.707106,-0.707106;3.13967rad)
  diameter = 1
  invert = false
  matchOuter = false
  offset = 0
  thread = false
  type = 5
  expr: Placement = GripperBot_GripperBot.Placement * GripperBot#HoleAxis_8.Placement * AttachmentOffset
FEATURE [Part::FeaturePython] Nut013  label="M3-Nut216"  # Fasteners workbench fastener (typed FeaturePython)
  AssemblyType = Asm4EE
  AttachedBy = Origin
  AttachedTo = GripperBot_GripperBot#HoleAxis_3
  AttachmentOffset = pos=(0,0,0) rot=(0.707107,-0.707107,0;3.14159rad)
  Placement = pos=(21.0148,-5.39284,66.5) rot=(0.576826,0.578398,-0.576826;2.09282rad)
  diameter = 4
  invert = false
  matchOuter = false
  offset = 0
  thread = false
  type = 7
  expr: Placement = GripperBot_GripperBot.Placement * GripperBot#HoleAxis_3.Placement * AttachmentOffset
FEATURE [Part::FeaturePython] Nut014  label="M3-Nut217"  # Fasteners workbench fastener (typed FeaturePython)
  AssemblyType = Asm4EE
  AttachedBy = Origin
  AttachedTo = GripperBot_GripperBot#HoleAxis_4
  AttachmentOffset = pos=(0,0,0) rot=(0.707107,-0.707107,0;3.14159rad)
  Placement = pos=(-20.9851,-5.50712,66.5) rot=(0.576826,0.578398,-0.576826;2.09282rad)
  diameter = 4
  invert = false
  matchOuter = false
  offset = 0
  thread = false
  type = 7
  expr: Placement = GripperBot_GripperBot.Placement * GripperBot#HoleAxis_4.Placement * AttachmentOffset
FEATURE [Part::FeaturePython] Nut015  label="M3-Nut214"  # Fasteners workbench fastener (typed FeaturePython)
  AssemblyType = Asm4EE
  AttachedBy = Origin
  AttachedTo = GripperBot_GripperBot#HoleAxis_6
  AttachmentOffset = pos=(0,0,0.6) rot=(0,0,1;0rad)
  Placement = pos=(29.1377,-8.32074,84) rot=(-0.000962,0.707106,-0.707106;3.13967rad)
  diameter = 4
  invert = false
  matchOuter = false
  offset = 0
  thread = false
  type = 7
  expr: Placement = GripperBot_GripperBot.Placement * GripperBot#HoleAxis_6.Placement * AttachmentOffset
FEATURE [Part::FeaturePython] Nut016  label="M3-Nut210"  # Fasteners workbench fastener (typed FeaturePython)
  AssemblyType = Asm4EE
  AttachedBy = Origin
  AttachedTo = GripperBot_GripperBot#HoleAxis_7
  AttachmentOffset = pos=(0,0,0.6) rot=(0,0,1;0rad)
  Placement = pos=(29.1377,-8.32074,94) rot=(-0.000962,0.707106,-0.707106;3.13967rad)
  diameter = 4
  invert = false
  matchOuter = false
  offset = 0
  thread = false
  type = 7
  expr: Placement = GripperBot_GripperBot.Placement * GripperBot#HoleAxis_7.Placement * AttachmentOffset
FEATURE [Part::FeaturePython] Nut017  label="M3-Nut211"  # Fasteners workbench fastener (typed FeaturePython)
  AssemblyType = Asm4EE
  AttachedBy = Origin
  AttachedTo = GripperBot_GripperBot#HoleAxis_11
  AttachmentOffset = pos=(0,0,0.6) rot=(0,0,1;0rad)
  Placement = pos=(-20.6621,-8.45626,84) rot=(-0.000962,0.707106,-0.707106;3.13967rad)
  diameter = 4
  invert = false
  matchOuter = false
  offset = 0
  thread = false
  type = 7
  expr: Placement = GripperBot_GripperBot.Placement * GripperBot#HoleAxis_11.Placement * AttachmentOffset
FEATURE [Part::FeaturePython] Nut018  label="M3-Nut212"  # Fasteners workbench fastener (typed FeaturePython)
  AssemblyType = Asm4EE
  AttachedBy = Origin
  AttachedTo = GripperBot_GripperBot#HoleAxis_10
  AttachmentOffset = pos=(0,0,0.6) rot=(0,0,1;0rad)
  Placement = pos=(-20.6621,-8.45626,94) rot=(-0.000962,0.707106,-0.707106;3.13967rad)
  diameter = 4
  invert = false
  matchOuter = false
  offset = 0
  thread = false
  type = 7
  expr: Placement = GripperBot_GripperBot.Placement * GripperBot#HoleAxis_10.Placement * AttachmentOffset
FEATURE [Part::FeaturePython] Nut006  label="M3-Nut222"  # Fasteners workbench fastener (typed FeaturePython)
  AssemblyType = Asm4EE
  AttachedBy = Origin
  AttachedTo = GripperBot_GripperBot#HoleAxis_5
  AttachmentOffset = pos=(0,0,0) rot=(0.707107,-0.707107,0;3.14159rad)
  Placement = pos=(-14.4851,-5.48944,89) rot=(-0.576826,-0.578398,0.576826;4.19036rad)
  diameter = 1
  invert = false
  matchOuter = false
  offset = 0
  thread = false
  type = 5
  expr: Placement = GripperBot_GripperBot.Placement * GripperBot#HoleAxis_5.Placement * AttachmentOffset
FEATURE [Part::FeaturePython] Screw010  label="M3x20-Screw041"  # Fasteners workbench fastener (typed FeaturePython)
  AssemblyType = Asm4EE
  AttachedBy = Origin
  AttachedTo = Unnamed_GripperTop#HoleAxis_5
  AttachmentOffset = pos=(0,0,0) rot=(1,0,0;3.14159rad)
  Placement = pos=(-6.01263,4.63366,107.5) rot=(-0.000962,0.707106,0.707106;3.14352rad)
  diameter = 4
  invert = false
  length = 7
  lengthCustom = 20
  matchOuter = false
  offset = 0
  thread = false
  type = 33
  expr: Placement = Unnamed_GripperTop.Placement * GripperTop#HoleAxis_5.Placement * AttachmentOffset
FEATURE [Part::FeaturePython] Screw011  label="M3x20-Screw"  # Fasteners workbench fastener (typed FeaturePython)
  AssemblyType = Asm4EE
  AttachedBy = Origin
  AttachedTo = Unnamed_GripperTop#HoleAxis_6
  AttachmentOffset = pos=(0,0,0) rot=(1,0,0;3.14159rad)
  Placement = pos=(5.98732,4.66631,107.5) rot=(-0.000962,0.707106,0.707106;3.14352rad)
  diameter = 4
  invert = false
  length = 7
  lengthCustom = 20
  matchOuter = false
  offset = 0
  thread = false
  type = 33
  expr: Placement = Unnamed_GripperTop.Placement * GripperTop#HoleAxis_6.Placement * AttachmentOffset
FEATURE [Part::FeaturePython] Screw012  label="M3x20-Screw042"  # Fasteners workbench fastener (typed FeaturePython)
  AssemblyType = Asm4EE
  AttachedBy = Origin
  AttachedTo = Unnamed_GripperTop#HoleAxis_2
  AttachmentOffset = pos=(0,0,0) rot=(1,0,0;3.14159rad)
  Placement = pos=(-21.0289,10.5928,66.5) rot=(-0.000962,0.707106,0.707106;3.14352rad)
  diameter = 4
  invert = false
  length = 7
  lengthCustom = 20
  matchOuter = false
  offset = 0
  thread = false
  type = 33
  expr: Placement = Unnamed_GripperTop.Placement * GripperTop#HoleAxis_2.Placement * AttachmentOffset
FEATURE [Part::FeaturePython] Screw013  label="M3x20-Screw043"  # Fasteners workbench fastener (typed FeaturePython)
  AssemblyType = Asm4EE
  AttachedBy = Origin
  AttachedTo = Unnamed_GripperTop#HoleAxis_3
  AttachmentOffset = pos=(0,0,0) rot=(1,0,0;3.14159rad)
  Placement = pos=(20.9709,10.7071,66.5) rot=(-0.000962,0.707106,0.707106;3.14352rad)
  diameter = 4
  invert = false
  length = 7
  lengthCustom = 20
  matchOuter = false
  offset = 0
  thread = false
  type = 33
  expr: Placement = Unnamed_GripperTop.Placement * GripperTop#HoleAxis_3.Placement * AttachmentOffset
FEATURE [Part::FeaturePython] Screw014  label="M3x12-Screw159"  # Fasteners workbench fastener (typed FeaturePython)
  AssemblyType = Asm4EE
  AttachedBy = Origin
  AttachedTo = Servomotor001#HoleAxis_1
  AttachmentOffset = pos=(0,0,0) rot=(1,0,0;3.14159rad)
  Placement = pos=(29.1588,-19.8707,94) rot=(0.914981,0.286558,-0.284067;1.65869rad)
  diameter = 4
  invert = false
  length = 4
  lengthCustom = 12
  matchOuter = false
  offset = 0
  thread = false
  type = 33
  expr: Placement = Servomotor001.Placement * HoleAxis_1.Placement * AttachmentOffset
FEATURE [Part::FeaturePython] Screw015  label="M3x12-Screw161"  # Fasteners workbench fastener (typed FeaturePython)
  AssemblyType = Asm4EE
  AttachedBy = Origin
  AttachedTo = Servomotor001#HoleAxis_2
  Placement = pos=(29.1588,-19.8707,84) rot=(-0.915108,0.283865,-0.286354;4.62295rad)
  diameter = 4
  invert = false
  length = 4
  lengthCustom = 12
  matchOuter = false
  offset = 0
  thread = false
  type = 33
  expr: Placement = Servomotor001.Placement * HoleAxis_2.Placement * AttachmentOffset
FEATURE [Part::FeaturePython] Screw016  label="M3x12-Screw160"  # Fasteners workbench fastener (typed FeaturePython)
  AssemblyType = Asm4EE
  AttachedBy = Origin
  AttachedTo = Servomotor001#HoleAxis_3
  Placement = pos=(-20.6203,-20.0062,94) rot=(0.214337,0.690966,-0.690381;2.71572rad)
  diameter = 4
  invert = false
  length = 4
  lengthCustom = 12
  matchOuter = false
  offset = 0
  thread = false
  type = 33
  expr: Placement = Servomotor001.Placement * HoleAxis_3.Placement * AttachmentOffset
FEATURE [Part::FeaturePython] Screw017  label="M3x12-Screw158"  # Fasteners workbench fastener (typed FeaturePython)
  AssemblyType = Asm4EE
  AttachedBy = Origin
  AttachedTo = Servomotor001#HoleAxis_4
  AttachmentOffset = pos=(0,0,0) rot=(1,0,0;3.14159rad)
  Placement = pos=(-20.6203,-20.0062,84) rot=(0.216129,-0.690101,0.690687;2.71947rad)
  diameter = 4
  invert = false
  length = 4
  lengthCustom = 12
  matchOuter = false
  offset = 0
  thread = false
  type = 33
  expr: Placement = Servomotor001.Placement * HoleAxis_4.Placement * AttachmentOffset
FEATURE [Part::FeaturePython] Screw018  label="M3x12-Screw148"  # Fasteners workbench fastener (typed FeaturePython)
  AssemblyType = Asm4EE
  AttachedBy = Origin
  AttachedTo = Unnamed_GripperTop#HoleAxis_4
  AttachmentOffset = pos=(0,0,0) rot=(1,0,0;3.14159rad)
  Placement = pos=(-14.5126,4.61053,89) rot=(-0.000962,0.707106,0.707106;3.14352rad)
  diameter = 4
  invert = false
  length = 4
  lengthCustom = 12
  matchOuter = false
  offset = 0
  thread = false
  type = 33
  expr: Placement = Unnamed_GripperTop.Placement * GripperTop#HoleAxis_4.Placement * AttachmentOffset
FEATURE [Part::FeaturePython] Screw019  label="M3x12-Screw155"  # Fasteners workbench fastener (typed FeaturePython)
  AssemblyType = Asm4EE
  AttachedBy = Origin
  AttachedTo = Unnamed_GripperTop#HoleAxis_1
  Placement = pos=(-0.048028,17.6499,59.5) rot=(-0.000962,0.707106,0.707106;3.14352rad)
  diameter = 4
  invert = false
  length = 4
  lengthCustom = 12
  matchOuter = false
  offset = 0
  thread = false
  type = 33
  expr: Placement = Unnamed_GripperTop.Placement * GripperTop#HoleAxis_1.Placement * AttachmentOffset
FEATURE [Part::FeaturePython] Screw020  label="M3x12-Screw147"  # Fasteners workbench fastener (typed FeaturePython)
  AssemblyType = Asm4EE
  AttachedBy = Origin
  AttachedTo = GripperBot_GripperBot#HoleAxis_1
  AttachmentOffset = pos=(0,0,0) rot=(1,0,0;3.14159rad)
  Placement = pos=(-17.2228,-10.0062,59.5) rot=(0.376947,0.654947,-0.654947;3.86254rad)
  diameter = 4
  invert = false
  length = 4
  lengthCustom = 12
  matchOuter = false
  offset = 0
  thread = false
  type = 33
  expr: Placement = GripperBot_GripperBot.Placement * GripperBot#HoleAxis_1.Placement * AttachmentOffset
FEATURE [Part::FeaturePython] Screw021  label="M3x12-Screw156"  # Fasteners workbench fastener (typed FeaturePython)
  AssemblyType = Asm4EE
  AttachedBy = Origin
  AttachedTo = GripperBot_GripperBot#HoleAxis_2
  AttachmentOffset = pos=(0,0,0) rot=(1,0,0;3.14159rad)
  Placement = pos=(17.277,-9.91232,59.5) rot=(0.773623,0.448056,0.448056;1.82469rad)
  diameter = 4
  invert = false
  length = 4
  lengthCustom = 12
  matchOuter = false
  offset = 0
  thread = false
  type = 33
  expr: Placement = GripperBot_GripperBot.Placement * GripperBot#HoleAxis_2.Placement * AttachmentOffset
FEATURE [App::Link] Unnamed1_GripperFinger
  AssemblyType = Asm4EE
  AttachedBy = #LCS_GripperFinger
  AttachedTo = Unnamed2_GripperArm001#LCS_GripperArm_1
  AttachmentOffset = pos=(0,0,0) rot=(0,0,1;4.71239rad)
  LinkPlacement = pos=(53.5208,-7.57939,85) rot=(0.000962,-0.707106,-0.707106;3.13967rad)
  LinkedObject = -> <external GripperFinger.FCStd>#Body
  Placement = pos=(53.5208,-7.57939,85) rot=(0.000962,-0.707106,-0.707106;3.13967rad)
  expr: Placement = Unnamed2_GripperArm001.Placement * GripperArm#LCS_GripperArm_1.Placement * AttachmentOffset * GripperFinger#LCS_GripperFinger.Placement ^ -1
FEATURE [PartDesign::CoordinateSystem] LCS_GripperFinger_sym
  AttacherType = Attacher::AttachEngine3D
  MapMode = 2
  Support = -> [X_Axis007]
FEATURE [App::Link] Unnamed1_GripperFinger_link
  LinkedObject = -> Unnamed1_GripperFinger
FEATURE [Part::Mirroring] Unnamed1_GripperFinger_mirrored
  Base = (0,0,0)
  Normal = (1,0,0)
  Source = -> Unnamed1_GripperFinger_link
FEATURE [PartDesign::CoordinateSystem] LCS_GripperFinger_sym001
  AttacherType = Attacher::AttachEngine3D
  MapMode = 11
  Placement = pos=(-12.5,22.5,5.075) rot=(0.707107,0.707107,0;3.14159rad)
  Support = -> [Unnamed1_GripperFinger_mirrored]
FEATURE [PartDesign::Line] HoleAxis_5
  AttacherType = Attacher::AttachEngineLine
  Length = 4.79083
  MapMode = 19
  Placement = pos=(-12.5,22.5,12.5) rot=(0,1,0;3.14159rad)
  ResizeMode = 1
  Support = -> [Unnamed1_GripperFinger_mirrored]
FEATURE [PartDesign::Line] HoleAxis_6
  AttacherType = Attacher::AttachEngineLine
  Length = 4.79083
  MapMode = 19
  Placement = pos=(-4,4,12.5) rot=(0,1,0;3.14159rad)
  ResizeMode = 1
  Support = -> [Unnamed1_GripperFinger_mirrored]
FEATURE [PartDesign::Line] HoleAxis_7
  AttacherType = Attacher::AttachEngineLine
  Length = 4.79083
  MapMode = 19
  Placement = pos=(-4,4,3) rot=(0,1,0;3.14159rad)
  ResizeMode = 1
  Support = -> [Unnamed1_GripperFinger_mirrored]
FEATURE [PartDesign::Line] HoleAxis_8
  AttacherType = Attacher::AttachEngineLine
  Length = 4.79083
  MapMode = 19
  Placement = pos=(-12.5,22.5,3) rot=(0,1,0;3.14159rad)
  ResizeMode = 1
  Support = -> [Unnamed1_GripperFinger_mirrored]
FEATURE [App::Part] GripperFinger_sym
  Group = -> [LCS_GripperFinger_sym,Unnamed1_GripperFinger_link,Unnamed1_GripperFinger_mirrored,LCS_GripperFinger_sym001,HoleAxis_5,HoleAxis_6,HoleAxis_7,HoleAxis_8]
  Origin = -> Origin007
FEATURE [App::DocumentObjectGroup] Group005  label="3DParts"
  Group = -> [GripperFinger_sym]
FEATURE [App::DocumentObjectGroup] Parts
  Group = -> [Group002,Group,Group004,Group005]
FEATURE [App::Link] GripperFinger_sym001
  AssemblyType = Asm4EE
  AttachedBy = #LCS_GripperFinger_sym001
  AttachedTo = Unnamed2_GripperArm#LCS_GripperArm_1
  AttachmentOffset = pos=(0,0,0) rot=(-0.707107,-0.707107,0;3.14159rad)
  LinkPlacement = pos=(-53.4788,-7.87055,85) rot=(0.000962,-0.707106,-0.707106;3.13967rad)
  LinkedObject = -> GripperFinger_sym
  Placement = pos=(-53.4788,-7.87055,85) rot=(0.000962,-0.707106,-0.707106;3.13967rad)
  expr: Placement = Unnamed2_GripperArm.Placement * GripperArm#LCS_GripperArm_1.Placement * AttachmentOffset * LCS_GripperFinger_sym001.Placement ^ -1
FEATURE [Part::FeaturePython] Nut019  label="M3-Nut221"  # Fasteners workbench fastener (typed FeaturePython)
  AssemblyType = Asm4EE
  AttachedBy = Origin
  AttachedTo = GripperFinger_sym001#HoleAxis_7
  AttachmentOffset = pos=(0,0,0) rot=(0,0,1;1.5708rad)
  Placement = pos=(-49.487,-4.85968,89) rot=(0.577873,-0.576303,0.577873;2.09597rad)
  diameter = 1
  invert = false
  matchOuter = false
  offset = 0
  thread = false
  type = 5
  expr: Placement = GripperFinger_sym001.Placement * HoleAxis_7.Placement * AttachmentOffset
FEATURE [Part::FeaturePython] Nut020  label="M3-Nut209"  # Fasteners workbench fastener (typed FeaturePython)
  AssemblyType = Asm4EE
  AttachedBy = Origin
  AttachedTo = GripperFinger_sym001#LCS_GripperFinger_sym001
  AttachmentOffset = pos=(0,0,0) rot=(0,0,1;1.5708rad)
  Placement = pos=(-40.9926,-2.76156,107.5) rot=(-0.000962,0.707106,-0.707106;3.13967rad)
  diameter = 1
  invert = false
  matchOuter = false
  offset = 0
  thread = false
  type = 5
  expr: Placement = GripperFinger_sym001.Placement * LCS_GripperFinger_sym001.Placement * AttachmentOffset
FEATURE [Part::FeaturePython] Nut021  label="M3-Nut208"  # Fasteners workbench fastener (typed FeaturePython)
  AssemblyType = Asm4EE
  AttachedBy = Origin
  AttachedTo = Unnamed1_GripperFinger#HoleAxis_3
  AttachmentOffset = pos=(0,0,0) rot=(0.707107,-0.707107,0;3.14159rad)
  Placement = pos=(49.5127,-4.59029,89) rot=(0.576826,0.578398,-0.576826;2.09282rad)
  diameter = 1
  invert = false
  matchOuter = false
  offset = 0
  thread = false
  type = 5
  expr: Placement = Unnamed1_GripperFinger.Placement * GripperFinger#HoleAxis_3.Placement * AttachmentOffset
FEATURE [Part::FeaturePython] Nut022  label="M3-Nut220"  # Fasteners workbench fastener (typed FeaturePython)
  AssemblyType = Asm4EE
  AttachedBy = Origin
  AttachedTo = Unnamed1_GripperFinger#HoleAxis_4
  AttachmentOffset = pos=(0,0,0) rot=(0.707107,-0.707107,0;3.14159rad)
  Placement = pos=(41.0127,-4.61342,107.5) rot=(0.576826,0.578398,-0.576826;2.09282rad)
  diameter = 1
  invert = false
  matchOuter = false
  offset = 0
  thread = false
  type = 5
  expr: Placement = Unnamed1_GripperFinger.Placement * GripperFinger#HoleAxis_4.Placement * AttachmentOffset
FEATURE [Part::FeaturePython] Screw022  label="M3x12-Screw"  # Fasteners workbench fastener (typed FeaturePython)
  AssemblyType = Asm4EE
  AttachedBy = Origin
  AttachedTo = Unnamed1_GripperFinger#HoleAxis_1
  Placement = pos=(49.4868,4.90968,89) rot=(-0.000962,0.707106,0.707106;3.14352rad)
  diameter = 4
  invert = false
  length = 4
  lengthCustom = 12
  matchOuter = false
  offset = 0
  thread = false
  type = 33
  expr: Placement = Unnamed1_GripperFinger.Placement * GripperFinger#HoleAxis_1.Placement * AttachmentOffset
FEATURE [Part::FeaturePython] Screw023  label="M3x12-Screw157"  # Fasteners workbench fastener (typed FeaturePython)
  AssemblyType = Asm4EE
  AttachedBy = Origin
  AttachedTo = Unnamed1_GripperFinger#HoleAxis_2
  Placement = pos=(40.9869,4.88655,107.5) rot=(-0.000962,0.707106,0.707106;3.14352rad)
  diameter = 4
  invert = false
  length = 4
  lengthCustom = 12
  matchOuter = false
  offset = 0
  thread = false
  type = 33
  expr: Placement = Unnamed1_GripperFinger.Placement * GripperFinger#HoleAxis_2.Placement * AttachmentOffset
FEATURE [Part::FeaturePython] Screw024  label="M3x12-Screw150"  # Fasteners workbench fastener (typed FeaturePython)
  AssemblyType = Asm4EE
  AttachedBy = Origin
  AttachedTo = GripperFinger_sym001#HoleAxis_6
  AttachmentOffset = pos=(0,0,0) rot=(1,0,0;3.14159rad)
  Placement = pos=(-49.5128,4.64029,89) rot=(-0.999998,-0.001361,0.001361;1.5708rad)
  diameter = 4
  invert = false
  length = 4
  lengthCustom = 12
  matchOuter = false
  offset = 0
  thread = false
  type = 33
  expr: Placement = GripperFinger_sym001.Placement * HoleAxis_6.Placement * AttachmentOffset
FEATURE [Part::FeaturePython] Screw025  label="M3x12-Screw152"  # Fasteners workbench fastener (typed FeaturePython)
  AssemblyType = Asm4EE
  AttachedBy = Origin
  AttachedTo = GripperFinger_sym001#HoleAxis_5
  AttachmentOffset = pos=(0,0,0) rot=(1,0,0;3.14159rad)
  Placement = pos=(-41.0128,4.66342,107.5) rot=(-0.999998,-0.001361,0.001361;1.5708rad)
  diameter = 4
  invert = false
  length = 4
  lengthCustom = 12
  matchOuter = false
  offset = 0
  thread = false
  type = 33
  expr: Placement = GripperFinger_sym001.Placement * HoleAxis_5.Placement * AttachmentOffset
FEATURE [Part::FeaturePython] Screw026  label="M2x4-Screw"  # Fasteners workbench fastener (typed FeaturePython)
  AssemblyType = Asm4EE
  AttachedBy = Origin
  AttachedTo = GripperActiveArm_GripperActiveArm#HoleAxis_3
  AttachmentOffset = pos=(0,0,0) rot=(1,0,0;3.14159rad)
  Placement = pos=(14.5463,1.08959,82.0001) rot=(-0.999992,-0.003801,-0.00108;1.5708rad)
  diameter = 2
  invert = false
  length = 1
  lengthCustom = 4
  matchOuter = false
  offset = 0
  thread = false
  type = 34
  expr: Placement = GripperActiveArm_GripperActiveArm.Placement * GripperActiveArm#HoleAxis_3.Placement * AttachmentOffset
FEATURE [Part::FeaturePython] Screw027  label="M2x6-Screw"  # Fasteners workbench fastener (typed FeaturePython)
  AssemblyType = Asm4EE
  AttachedBy = Origin
  AttachedTo = GripperActiveArm_GripperActiveArm#HoleAxis_2
  Placement = pos=(14.5121,1.08949,89) rot=(-0.999992,-0.003801,-0.00108;1.5708rad)
  diameter = 2
  invert = false
  length = 3
  lengthCustom = 6
  matchOuter = false
  offset = 0
  thread = false
  type = 34
  expr: Placement = GripperActiveArm_GripperActiveArm.Placement * GripperActiveArm#HoleAxis_2.Placement * AttachmentOffset
FEATURE [Part::FeaturePython] Screw028  label="M2x4-Screw001"  # Fasteners workbench fastener (typed FeaturePython)
  AssemblyType = Asm4EE
  AttachedBy = Origin
  AttachedTo = GripperActiveArm_GripperActiveArm#HoleAxis_1
  AttachmentOffset = pos=(0,0,0) rot=(1,0,0;3.14159rad)
  Placement = pos=(14.4779,1.0894,95.9999) rot=(-0.999992,-0.003801,-0.00108;1.5708rad)
  diameter = 2
  invert = false
  length = 1
  lengthCustom = 4
  matchOuter = false
  offset = 0
  thread = false
  type = 34
  expr: Placement = GripperActiveArm_GripperActiveArm.Placement * GripperActiveArm#HoleAxis_1.Placement * AttachmentOffset
FEATURE [App::DocumentObjectGroup] Group003  label="Fasteners"
  Group = -> [Nut001,Nut002,Nut004,Nut003,Nut,Screw,Screw003,Screw002,Screw001,Screw004,Nut005,Nut012,Nut011,Nut014,Nut013,Nut015,Nut016,Nut017,Nut018,Nut006,Screw010,Screw011,Screw012,Screw013,Screw014,Screw015,Screw016,Screw017,Screw018,Screw019,Screw020,Screw021,Nut020,Nut021,Nut022,Nut019,Screw023,Screw024,Screw025,Screw022,Screw028,Screw027,Screw026]
FEATURE [App::Part] Model
  Configuration = 0
  Group = -> [LCS_Origin,Constraints,Variables,Art56MotorCoverRing_Art56MotorCoverRing,CommonBearingFixThrough_CommonBearingFixThrough,Art56GearPlate_Art56GearPlate,Art56SmallGear_Art56SmallGear,Art56SmallGear_Art56SmallGear001,Bearing_625ZZ001,Bearing_625ZZ002,Pulley_GT2x40001,Pulley_GT2x40002,LCS_Art4Fix,GripperBot_GripperBot,Unnamed_GripperTop,Servomotor001,ServomotorWheelHorn001,+50 more]
  Origin = -> Origin
  Type = Assembly4 Model
---- part AssemblyBase.FCStd = doc fcstd_1964b144c772 (69587 chars; too large to inline — full recipe in that document) ----
